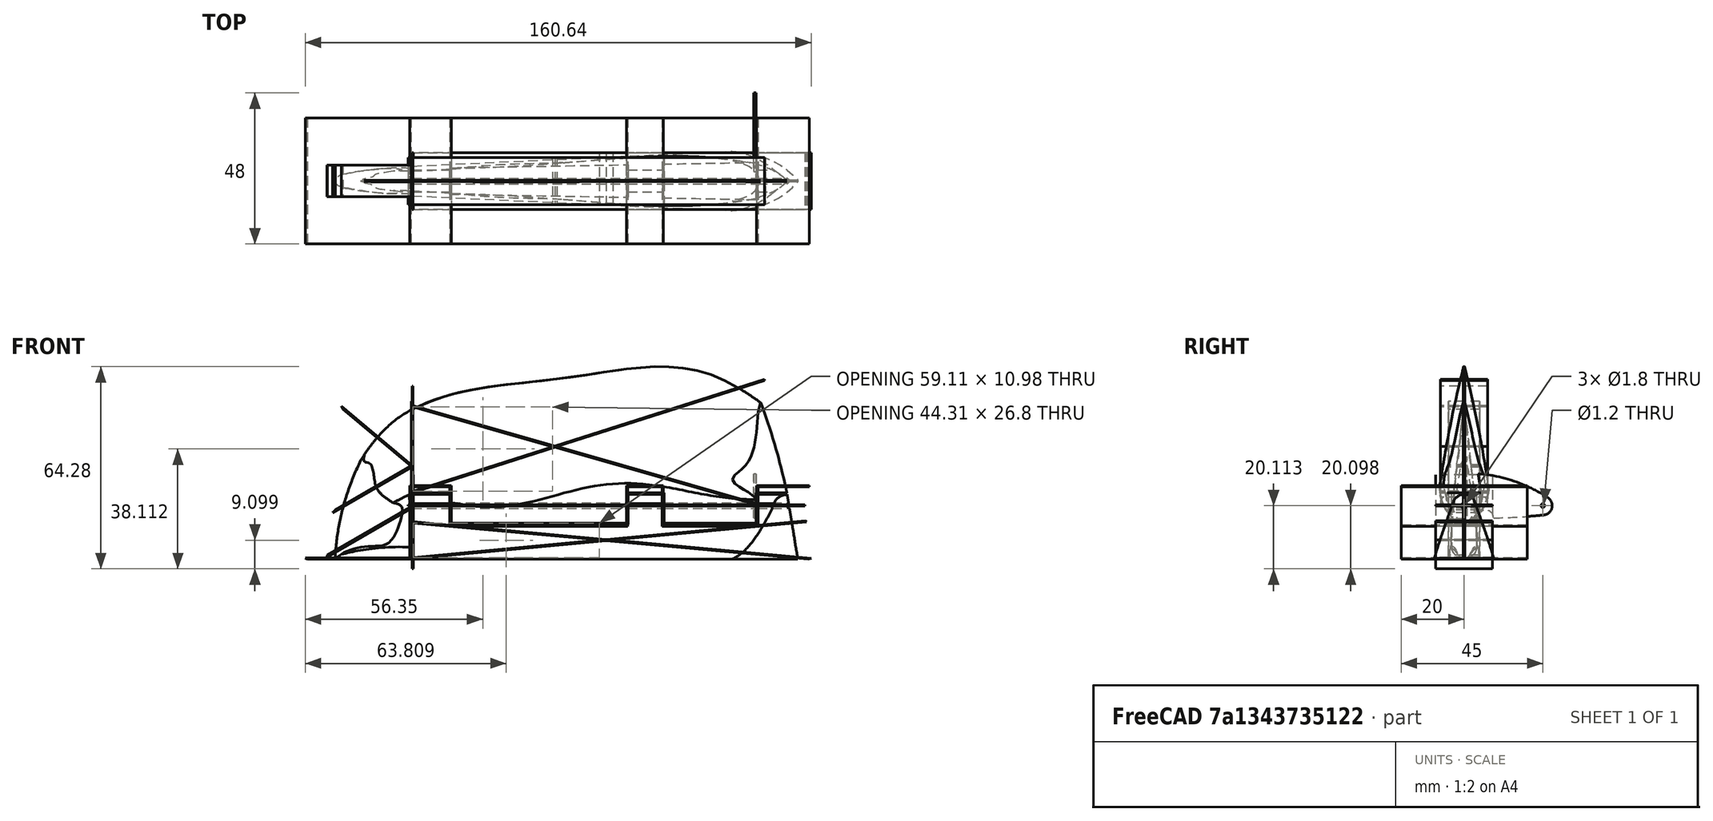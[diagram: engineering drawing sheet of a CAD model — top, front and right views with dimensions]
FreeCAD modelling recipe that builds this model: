
FCSTD DOCUMENT  (FreeCAD 0.20R29410 (Git))
Label: ruddersplit
License: All rights reserved
LicenseURL: http://en.wikipedia.org/wiki/All_rights_reserved
objects: Sketcher::SketchObject×34, PartDesign::Plane×8, PartDesign::Body×8, Mesh::Feature×7, PartDesign::Pad×5, PartDesign::Pocket×5, PartDesign::ShapeBinder×4, PartDesign::AdditiveLoft×3, PartDesign::SubtractiveLoft×3, PartDesign::FeatureBase×1, App::Part×1
note: 87 computed .brp shape members not serialized (recipe doc carries the construction recipe); baked Part::Feature solids carry a one-line shape summary decoded from their .brp

FEATURE [Mesh::Feature] Ta152_rudder  label="Ta152 rudder"
FEATURE [Sketcher::SketchObject] Sketch
  FullyConstrained = false
  MapMode = 5
  Placement = pos=(0,0,0) rot=(1,0,0;1.5708rad)
  Support = -> [XZ_Plane]
  sketch-geometry (24):
    g0: LineSegment StartX=624.263 StartY=141.903 StartZ=0 EndX=657.263 EndY=141.903 EndZ=0
    g1: LineSegment StartX=657.263 StartY=141.903 StartZ=0 EndX=657.263 EndY=164.903 EndZ=0
    g2: LineSegment StartX=657.263 StartY=164.903 StartZ=0 EndX=669.563 EndY=164.903 EndZ=0
    g3: LineSegment StartX=669.563 StartY=164.903 StartZ=0 EndX=669.563 EndY=152.313 EndZ=0
    g4: LineSegment StartX=669.563 StartY=152.313 StartZ=0 EndX=726.093 EndY=152.313 EndZ=0
    g5: LineSegment StartX=726.093 StartY=152.313 StartZ=0 EndX=726.093 EndY=164.903 EndZ=0
    g6: LineSegment StartX=726.093 StartY=164.903 StartZ=0 EndX=736.993 EndY=164.903 EndZ=0
    g7: LineSegment StartX=736.993 StartY=164.903 StartZ=0 EndX=736.993 EndY=152.313 EndZ=0
    g8: LineSegment StartX=736.993 StartY=152.313 StartZ=0 EndX=767.393 EndY=152.313 EndZ=0
    g9: LineSegment StartX=767.393 StartY=152.313 StartZ=0 EndX=767.393 EndY=164.903 EndZ=0
    g10: LineSegment StartX=767.393 StartY=164.903 StartZ=0 EndX=783.71 EndY=164.903 EndZ=0
    g11: LineSegment StartX=624.263 StartY=141.903 StartZ=0 EndX=623.694 EndY=142.303 EndZ=0
    g12: LineSegment StartX=623.694 StartY=142.303 StartZ=0 EndX=656.863 EndY=142.303 EndZ=0
    g13: LineSegment StartX=656.863 StartY=142.303 StartZ=0 EndX=656.863 EndY=165.303 EndZ=0
    g14: LineSegment StartX=656.863 StartY=165.303 StartZ=0 EndX=670.063 EndY=165.303 EndZ=0
    g15: LineSegment StartX=670.063 StartY=165.303 StartZ=0 EndX=670.063 EndY=152.713 EndZ=0
    g16: LineSegment StartX=670.063 StartY=152.713 StartZ=0 EndX=725.693 EndY=152.713 EndZ=0
    g17: LineSegment StartX=725.693 StartY=152.713 StartZ=0 EndX=725.693 EndY=165.303 EndZ=0
    g18: LineSegment StartX=725.693 StartY=165.303 StartZ=0 EndX=737.393 EndY=165.303 EndZ=0
    g19: LineSegment StartX=737.393 StartY=165.303 StartZ=0 EndX=737.393 EndY=152.713 EndZ=0
    g20: LineSegment StartX=737.393 StartY=152.713 StartZ=0 EndX=766.993 EndY=152.713 EndZ=0
    g21: LineSegment StartX=766.993 StartY=152.713 StartZ=0 EndX=766.993 EndY=165.303 EndZ=0
    g22: LineSegment StartX=766.993 StartY=165.303 StartZ=0 EndX=783.71 EndY=165.303 EndZ=0
    g23: LineSegment StartX=783.71 StartY=165.303 StartZ=0 EndX=783.71 EndY=164.903 EndZ=0
  constraints (70):
    c: Coincident(g0,g1)
    c: Coincident(g1,g2)
    c: Horizontal(g2)
    c: Coincident(g2,g3)
    c: Coincident(g3,g4)
    c: Horizontal(g4)
    c: Coincident(g4,g5)
    c: Coincident(g5,g6)
    c: Horizontal(g6)
    c: Coincident(g6,g7)
    c: Vertical(g7)
    c: Coincident(g7,g8)
    c: Horizontal(g8)
    c: Coincident(g8,g9)
    c: Vertical(g9)
    c: Coincident(g9,g10)
    c: Horizontal(g10)
    c: Vertical(g1)
    c: Vertical(g3)
    c: Vertical(g5)
    c: Horizontal(g0)
    c: Horizontal(g4,g7)
    c: Horizontal(g9,g6)
    c: Horizontal(g5,g2)
    c: Coincident(g0,g11)
    c: Coincident(g11,g12)
    c: Horizontal(g12)
    c: Coincident(g12,g13)
    c: Vertical(g13)
    c: Coincident(g13,g14)
    c: Horizontal(g14)
    c: Coincident(g14,g15)
    c: Vertical(g15)
    c: Coincident(g15,g16)
    c: Horizontal(g16)
    c: Coincident(g16,g17)
    c: Vertical(g17)
    c: Coincident(g17,g18)
    c: Horizontal(g18)
    c: Coincident(g18,g19)
    c: Vertical(g19)
    c: Coincident(g19,g20)
    c: Horizontal(g20)
    c: Coincident(g20,g21)
    c: Vertical(g21)
    c: Coincident(g21,g22)
    c: Horizontal(g22)
    c: Coincident(g22,g23)
    c: Coincident(g23,g10)
    c: Vertical(g23)
    c: DistanceY(g0,g12) = 0.4
    c: DistanceX(g13,g1) = 0.4
    c: DistanceX(g2,g14) = 0.5
    c: DistanceY(g1,g13) = 0.4
    c: DistanceY(g3,g15) = 0.4
    c: DistanceX(g17,g5) = 0.4
    c: DistanceX(g6,g18) = 0.4
    c: Horizontal(g16,g19)
    c: Horizontal(g17,g14)
    c: Horizontal(g21,g18)
    c: DistanceX(g20,g8) = 0.4
    c: DistanceX(g0) = 624.263
    c: DistanceY(g0) = 141.903
    c: DistanceX(g0,g0) = 33  'Length1'
    c: DistanceY(g1,g1) = 23  'Height1'
    c: DistanceX(g2,g2) = 12.3  'Length2'
    c: DistanceY(g0,g3) = 10.41  'Hinge height'
    c: DistanceX(g4,g4) = 56.53  'Length3'
    c: DistanceX(g6,g6) = 10.9  'length4'
    c: DistanceX(g8,g8) = 30.4  'length5'
FEATURE [PartDesign::Pad] Pad
  Direction = (0,-1,-2e-16)
  Length = 40
  Length2 = 10
  Midplane = true
  Placement = pos=(0,0,0) rot=(1,0,0;1.5708rad)
  Profile = -> Sketch
  ReferenceAxis = -> Sketch [N_Axis]
  Type = 0
FEATURE [Sketcher::SketchObject] Sketch001
  FullyConstrained = true
  MapMode = 5
  Placement = pos=(624.263,-9e-16,141.903) rot=(0,1,0;3.14159rad)
FEATURE [PartDesign::Plane] DatumPlane001
  Length = 719.203
  MapMode = 7
  Placement = pos=(657.263,-20,141.903) rot=(0,1,0;3.14159rad)
  ResizeMode = 0
  Support = -> [Pad]
  Width = 86.9395
FEATURE [PartDesign::Plane] DatumPlane
  AttachmentOffset = pos=(-34,0,0) rot=(0,1,0;1.5708rad)
  Length = 68.2922
  MapMode = 45
  Placement = pos=(657.694,8.98e-14,142.303) rot=(-0.57735,0.57735,0.57735;4.18879rad)
  ResizeMode = 0
  Support = -> [Pad]
  Width = 185.595
FEATURE [Sketcher::SketchObject] Sketch002  label="Hingetop"
  FullyConstrained = false
  MapMode = 5
  Placement = pos=(657.694,8.98e-14,142.303) rot=(0.57735,-0.57735,-0.57735;2.0944rad)
  Support = -> [DatumPlane]
  sketch-geometry (5):
    g0: ArcOfCircle CenterX=0 CenterY=16.5851 CenterZ=0 NormalX=0 NormalY=0 NormalZ=1 AngleXU=0 Radius=3.59111 StartAngle=0.199351 EndAngle=2.94224
    g1: LineSegment StartX=-4.713 StartY=-0.4 StartZ=0 EndX=6.72755 EndY=-0.4 EndZ=0
    g2: LineSegment StartX=-3.51999 StartY=17.2962 StartZ=0 EndX=-4.713 EndY=-0.4 EndZ=0
    g3: LineSegment StartX=3.51999 StartY=17.2962 StartZ=0 EndX=4.713 EndY=-0.4 EndZ=0
    g4: LineSegment StartX=-4.713 StartY=-0.4 StartZ=0 EndX=4.713 EndY=-0.4 EndZ=0
  constraints (9):
    c: Horizontal(g0,g0)
    c: PointOnObject(g0,g-2)
    c: Horizontal(g1)
    c: DistanceY(g1,g-1) = 0.4
    c: Coincident(g2,g0)
    c: Coincident(g2,g1)
    c: Coincident(g4,g2)
    c: Coincident(g4,g3)
    c: Horizontal(g4)
FEATURE [Sketcher::SketchObject] Sketch003  label="Hingebottom"
  AttachmentOffset = pos=(0,0,-124) rot=(0,0,1;0rad)
  FullyConstrained = false
  MapMode = 5
  Placement = pos=(781.694,3.926e-13,142.303) rot=(0.57735,-0.57735,-0.57735;2.0944rad)
  Support = -> [DatumPlane]
  sketch-geometry (5):
    g0: ArcOfCircle CenterX=0 CenterY=16.5851 CenterZ=0 NormalX=0 NormalY=0 NormalZ=1 AngleXU=0 Radius=3.59111 StartAngle=0.199351 EndAngle=2.94224
    g1: LineSegment StartX=-9.5 StartY=-0.4 StartZ=0 EndX=6.72755 EndY=-0.4 EndZ=0
    g2: LineSegment StartX=-3.51999 StartY=17.2962 StartZ=0 EndX=-9.5 EndY=-0.4 EndZ=0
    g3: LineSegment StartX=3.51999 StartY=17.2962 StartZ=0 EndX=9.5 EndY=-0.4 EndZ=0
    g4: LineSegment StartX=-9.5 StartY=-0.4 StartZ=0 EndX=9.5 EndY=-0.4 EndZ=0
  constraints (10):
    c: Horizontal(g0,g0)
    c: PointOnObject(g0,g-2)
    c: Horizontal(g1)
    c: DistanceY(g1,g-1) = 0.4
    c: Coincident(g2,g0)
    c: Coincident(g2,g1)
    c: Coincident(g4,g2)
    c: Coincident(g4,g3)
    c: Symmetric(g2,g3,g-2)
    c: DistanceX(g4,g4) = 19
FEATURE [PartDesign::Body] Body
  Group = -> [Sketch,Pad,Sketch001,DatumPlane001,DatumPlane,Sketch002,Sketch003]
  Origin = -> Origin
  Tip = -> Pad
FEATURE [Sketcher::SketchObject] Sketch004  label="Hingetop001"
  FullyConstrained = false
  MapMode = 5
  Placement = pos=(657.694,8.98e-14,142.303) rot=(0.57735,-0.57735,-0.57735;2.0944rad)
  Support = -> [DatumPlane]
  sketch-geometry (6):
    g0: ArcOfCircle CenterX=0 CenterY=16.5851 CenterZ=0 NormalX=0 NormalY=0 NormalZ=1 AngleXU=0 Radius=3.59111 StartAngle=0.199351 EndAngle=2.94224
    g1: LineSegment StartX=-4.713 StartY=-0.4 StartZ=0 EndX=6.72755 EndY=-0.4 EndZ=0
    g2: LineSegment StartX=-3.51999 StartY=17.2962 StartZ=0 EndX=-4.713 EndY=-0.4 EndZ=0
    g3: LineSegment StartX=3.51999 StartY=17.2962 StartZ=0 EndX=4.713 EndY=-0.4 EndZ=0
    g4: LineSegment StartX=-4.713 StartY=-0.4 StartZ=0 EndX=4.713 EndY=-0.4 EndZ=0
    g5: Circle CenterX=0 CenterY=16.5851 CenterZ=0 NormalX=0 NormalY=0 NormalZ=1 AngleXU=0 Radius=0.9
  constraints (12):
    c: Horizontal(g0,g0)
    c: PointOnObject(g0,g-2)
    c: Horizontal(g1)
    c: DistanceY(g1,g-1) = 0.4
    c: Coincident(g2,g0)
    c: Coincident(g2,g1)
    c: Coincident(g4,g2)
    c: Coincident(g4,g3)
    c: Horizontal(g4)
    c: DistanceY(g0) = 16.5851
    c: Coincident(g5,g0)
    c: Diameter(g5) = 1.8
FEATURE [Sketcher::SketchObject] Sketch005  label="Hingebottom001"
  AttachmentOffset = pos=(0,0,-124) rot=(0,0,1;0rad)
  FullyConstrained = false
  MapMode = 5
  Placement = pos=(781.694,3.926e-13,142.303) rot=(0.57735,-0.57735,-0.57735;2.0944rad)
  Support = -> [DatumPlane]
  sketch-geometry (6):
    g0: ArcOfCircle CenterX=0 CenterY=16.5851 CenterZ=0 NormalX=0 NormalY=0 NormalZ=1 AngleXU=0 Radius=3.59111 StartAngle=0.199351 EndAngle=2.94224
    g1: LineSegment StartX=-10.5 StartY=-0.4 StartZ=0 EndX=6.72755 EndY=-0.4 EndZ=0
    g2: LineSegment StartX=-3.51999 StartY=17.2962 StartZ=0 EndX=-10.5 EndY=-0.4 EndZ=0
    g3: LineSegment StartX=3.51999 StartY=17.2962 StartZ=0 EndX=10.5 EndY=-0.4 EndZ=0
    g4: LineSegment StartX=-10.5 StartY=-0.4 StartZ=0 EndX=10.5 EndY=-0.4 EndZ=0
    g5: Circle CenterX=0 CenterY=16.5851 CenterZ=0 NormalX=0 NormalY=0 NormalZ=1 AngleXU=0 Radius=0.9
  constraints (13):
    c: Horizontal(g0,g0)
    c: PointOnObject(g0,g-2)
    c: Horizontal(g1)
    c: DistanceY(g1,g-1) = 0.4
    c: Coincident(g2,g0)
    c: Coincident(g2,g1)
    c: Coincident(g4,g2)
    c: Coincident(g4,g3)
    c: Symmetric(g2,g3,g-2)
    c: DistanceX(g4,g4) = 21
    c: DistanceY(g0) = 16.5851
    c: Coincident(g5,g0)
    c: Diameter(g5) = 1.8
FEATURE [PartDesign::Plane] CopyDatumPlane001
  Length = 719.203
  Placement = pos=(657.263,-20,141.903) rot=(0,1,0;3.14159rad)
  ResizeMode = 0
  Width = 86.9395
FEATURE [Sketcher::SketchObject] Sketch006
  FullyConstrained = false
  MapMode = 5
  Placement = pos=(657.263,-20,141.903) rot=(0,1,0;3.14159rad)
  Support = -> [CopyDatumPlane001]
  sketch-geometry (21):
    g0-g6: Circle x7 (B-spline internal-alignment scaffolding for g7; pole/knot coordinates omitted)
    g7: BSplineCurve PolesCount=7 KnotsCount=5 Degree=3 IsPeriodic=0
    g8-g11: GeomPoint x4 (B-spline internal-alignment scaffolding for g7; pole/knot coordinates omitted)
    g12: GeomPoint X=-122.781 Y=20.25 Z=0
    g13: LineSegment StartX=-122.783 StartY=20.25 StartZ=0 EndX=-122.783 EndY=19.7442 EndZ=0
    g14: LineSegment StartX=-83.4528 StartY=29.2883 StartZ=0 EndX=-83.4528 EndY=61.9285 EndZ=0
    g15: LineSegment StartX=-83.4528 StartY=61.9285 StartZ=0 EndX=-142.52 EndY=61.9285 EndZ=0
    g16: LineSegment StartX=-142.52 StartY=61.9285 StartZ=0 EndX=-142.52 EndY=-14.2649 EndZ=0
    g17: LineSegment StartX=-142.52 StartY=-14.2649 StartZ=0 EndX=-83.4528 EndY=-14.2649 EndZ=0
    g18: LineSegment StartX=-83.4528 StartY=-14.2649 StartZ=0 EndX=-83.4528 EndY=10.7059 EndZ=0
    g19: LineSegment StartX=-120.634 StartY=19.9971 StartZ=0 EndX=-124.073 EndY=19.9971 EndZ=0
    g20: BSplineCurve PolesCount=7 KnotsCount=5 Degree=3 IsPeriodic=0
  constraints (11):
    c: Weight(g0) = 1
    c: Equal(g0, g1-g6) x6
    c: InternalAlignment(g0-g6 -> g7) x7
    c: InternalAlignment(g8-g11 -> g7) x4
    c: Horizontal(g17)
    c: Coincident(g17,g18)
    c: Vertical(g18)
    c: Horizontal(g19)
    c: Symmetric(g13,g7,g19)
    c: Coincident(g20,g18)
    c: Coincident(g13,g20)
FEATURE [PartDesign::Plane] CopyDatumPlane002
  Length = 719.199
  Placement = pos=(657.26,-20,162.9) rot=(0,1,0;3.14159rad)
  ResizeMode = 0
  Width = 86.9394
FEATURE [Sketcher::SketchObject] Sketch007
  FullyConstrained = false
  MapMode = 5
  Placement = pos=(657.26,-20,162.9) rot=(0,1,0;3.14159rad)
  Support = -> [CopyDatumPlane002]
  sketch-geometry (21):
    g0-g3: Circle x4 (B-spline internal-alignment scaffolding for g4; pole/knot coordinates omitted)
    g4: BSplineCurve PolesCount=7 KnotsCount=5 Degree=3 IsPeriodic=0
    g5-g8: GeomPoint x4 (B-spline internal-alignment scaffolding for g4; pole/knot coordinates omitted)
    g9: Circle CenterX=-74.5909 CenterY=27.8004 CenterZ=0 NormalX=0 NormalY=0 NormalZ=1 AngleXU=0 Radius=1
    g10: Circle CenterX=-87.7384 CenterY=27.8332 CenterZ=0 NormalX=0 NormalY=0 NormalZ=1 AngleXU=0 Radius=1
    g11: Circle CenterX=-99.3594 CenterY=27.6151 CenterZ=0 NormalX=0 NormalY=0 NormalZ=1 AngleXU=0 Radius=1
    g12: GeomPoint X=-79.145 Y=27.8076 Z=0
    g13: LineSegment StartX=-119.344 StartY=20.2366 StartZ=0 EndX=-119.344 EndY=19.7468 EndZ=0
    g14: LineSegment StartX=-122.669 StartY=19.9917 StartZ=0 EndX=-115.003 EndY=19.9917 EndZ=0
    g15: BSplineCurve PolesCount=7 KnotsCount=5 Degree=3 IsPeriodic=0
    g16: LineSegment StartX=-68.8738 StartY=27.5511 StartZ=0 EndX=-68.8738 EndY=47.5798 EndZ=0
    g17: LineSegment StartX=-68.8738 StartY=47.5798 StartZ=0 EndX=-137.844 EndY=47.5798 EndZ=0
    g18: LineSegment StartX=-137.844 StartY=47.5798 StartZ=0 EndX=-137.844 EndY=-8.4859 EndZ=0
    g19: LineSegment StartX=-137.844 StartY=-8.4859 StartZ=0 EndX=-68.8738 EndY=-8.4859 EndZ=0
    g20: LineSegment StartX=-68.8738 StartY=-8.4859 StartZ=0 EndX=-68.8738 EndY=12.4323 EndZ=0
  constraints (25):
    c: Weight(g0) = 1
    c: Equal(g0,g1)
    c: Equal(g0,g2)
    c: Equal(g0,g3)
    c: InternalAlignment(g0-g3 -> g4) x4
    c: InternalAlignment(g5-g9 -> g4) x5
    c: Equal(g9,g0)
    c: InternalAlignment(g10,g4)
    c: Equal(g10,g0)
    c: Equal(g11,g0)
    c: InternalAlignment(g12,g4)
    c: Coincident(g13,g4)
    c: Horizontal(g14)
    c: Symmetric(g13,g4,g14)
    c: Coincident(g16,g4)
    c: Vertical(g16)
    c: Coincident(g16,g17)
    c: Horizontal(g17)
    c: Coincident(g17,g18)
    c: Vertical(g18)
    c: Coincident(g18,g19)
    c: Horizontal(g19)
    c: Coincident(g19,g20)
    c: Vertical(g20)
    c: Coincident(g15,g20)
FEATURE [Sketcher::SketchObject] Sketch008
  FullyConstrained = false
  MapMode = 5
  Placement = pos=(0,0,0) rot=(1,0,0;1.5708rad)
  Support = -> [XZ_Plane005]
  sketch-geometry (17):
    g0: LineSegment StartX=726.116 StartY=153.482 StartZ=0 EndX=726.116 EndY=229.788 EndZ=0
    g1: LineSegment StartX=669.49 StartY=153.672 StartZ=0 EndX=669.49 EndY=227.56 EndZ=0
    g2: LineSegment StartX=767.362 StartY=153.926 StartZ=0 EndX=767.362 EndY=224.102 EndZ=0
    g3: LineSegment StartX=725.987 StartY=152.316 StartZ=0 EndX=584.529 EndY=152.316 EndZ=0
    g4: LineSegment StartX=789.185 StartY=149.038 StartZ=0 EndX=782.856 EndY=164.717 EndZ=0
    g5: LineSegment StartX=782.856 StartY=164.717 StartZ=0 EndX=767.362 EndY=164.717 EndZ=0
    g6: LineSegment StartX=767.362 StartY=164.717 StartZ=0 EndX=767.362 EndY=152.912 EndZ=0
    g7: LineSegment StartX=767.362 StartY=152.912 StartZ=0 EndX=737.052 EndY=152.912 EndZ=0
    g8: LineSegment StartX=737.052 StartY=152.912 StartZ=0 EndX=737.052 EndY=166.962 EndZ=0
    g9: LineSegment StartX=737.052 StartY=166.962 StartZ=0 EndX=726.116 EndY=166.962 EndZ=0
    g10: LineSegment StartX=726.116 StartY=166.962 StartZ=0 EndX=726.116 EndY=152.912 EndZ=0
    g11: LineSegment StartX=726.116 StartY=152.912 StartZ=0 EndX=669.49 EndY=152.912 EndZ=0
    g12: LineSegment StartX=669.49 StartY=152.912 StartZ=0 EndX=669.49 EndY=166.268 EndZ=0
    g13: LineSegment StartX=669.49 StartY=166.268 StartZ=0 EndX=654.865 EndY=166.268 EndZ=0
    g14: LineSegment StartX=654.865 StartY=166.268 StartZ=0 EndX=654.865 EndY=181.772 EndZ=0
    g15: LineSegment StartX=654.865 StartY=181.772 StartZ=0 EndX=794.924 EndY=181.772 EndZ=0
    g16: LineSegment StartX=794.924 StartY=181.772 StartZ=0 EndX=789.185 EndY=149.038 EndZ=0
  constraints (32):
    c: Vertical(g0)
    c: Vertical(g1)
    c: Vertical(g2)
    c: Horizontal(g3)
    c: Coincident(g4,g5)
    c: PointOnObject(g5,g2)
    c: Horizontal(g5)
    c: Coincident(g5,g6)
    c: Vertical(g6)
    c: Coincident(g6,g7)
    c: Horizontal(g7)
    c: Coincident(g7,g8)
    c: Vertical(g8)
    c: Coincident(g8,g9)
    c: PointOnObject(g9,g0)
    c: Horizontal(g9)
    c: Coincident(g9,g10)
    c: Vertical(g10)
    c: Coincident(g10,g11)
    c: Horizontal(g11)
    c: Coincident(g11,g12)
    c: PointOnObject(g12,g1)
    c: Vertical(g12)
    c: Coincident(g12,g13)
    c: Horizontal(g13)
    c: Coincident(g13,g14)
    c: Vertical(g14)
    c: Coincident(g14,g15)
    c: Horizontal(g15)
    c: Coincident(g15,g16)
    c: Coincident(g16,g4)
    c: Horizontal(g10,g7)
FEATURE [Sketcher::SketchObject] Sketch017  label="SubLft2"
  AttachmentOffset = pos=(0,0,168) rot=(0,0,1;0rad)
  FullyConstrained = false
  MapMode = 5
  Placement = pos=(0,0,168) rot=(0,0,1;0rad)
  Support = -> [XY_Plane002]
  sketch-geometry (28):
    g0-g5: Circle x6 (B-spline internal-alignment scaffolding for g6; pole/knot coordinates omitted)
    g6: BSplineCurve PolesCount=6 KnotsCount=4 Degree=3 IsPeriodic=0
    g7-g10: GeomPoint x4 (B-spline internal-alignment scaffolding for g6; pole/knot coordinates omitted)
    g11-g16: Circle x6 (B-spline internal-alignment scaffolding for g17; pole/knot coordinates omitted)
    g17: BSplineCurve PolesCount=6 KnotsCount=4 Degree=3 IsPeriodic=0
    g18-g21: GeomPoint x4 (B-spline internal-alignment scaffolding for g17; pole/knot coordinates omitted)
    g22: LineSegment StartX=757.877 StartY=6.51924 StartZ=0 EndX=757.877 EndY=27.4666 EndZ=0
    g23: LineSegment StartX=757.877 StartY=27.4666 StartZ=0 EndX=799.809 EndY=27.4666 EndZ=0
    g24: LineSegment StartX=799.809 StartY=27.4666 StartZ=0 EndX=799.809 EndY=-22.2115 EndZ=0
    g25: LineSegment StartX=799.809 StartY=-22.2115 StartZ=0 EndX=757.877 EndY=-22.2115 EndZ=0
    g26: LineSegment StartX=757.877 StartY=-22.2115 StartZ=0 EndX=757.877 EndY=-6.51924 EndZ=0
    g27: LineSegment StartX=775.463 StartY=0.225 StartZ=0 EndX=775.463 EndY=-0.225 EndZ=0
  constraints (28):
    c: Weight(g0) = 1
    c: Equal(g0, g1-g5) x5
    c: InternalAlignment(g0-g5 -> g6) x6
    c: InternalAlignment(g7-g10 -> g6) x4
    c: Weight(g11) = 1
    c: Equal(g11, g12-g16) x5
    c: InternalAlignment(g11-g16 -> g17) x6
    c: InternalAlignment(g18-g21 -> g17) x4
    c: Symmetric(g15,g4,g-1)
    c: Symmetric(g3,g14,g-1)
    c: Symmetric(g2,g13,g-1)
    c: Symmetric(g12,g1,g-1)
    c: Coincident(g22,g6)
    c: Vertical(g22)
    c: Coincident(g22,g23)
    c: Horizontal(g23)
    c: Coincident(g23,g24)
    c: Vertical(g24)
    c: Coincident(g24,g25)
    c: Horizontal(g25)
    c: Coincident(g25,g26)
    c: Coincident(g26,g17)
    c: Vertical(g26)
    c: DistanceY(g27,g27) = 0.45
    c: Symmetric(g27,g27,g-1)
    c: Symmetric(g17,g6,g-1)
    c: Coincident(g6,g27)
    c: Symmetric(g6,g17,g-1)
FEATURE [Sketcher::SketchObject] Sketch018  label="SubLft3"
  AttachmentOffset = pos=(0,0,202) rot=(0,0,1;0rad)
  FullyConstrained = false
  MapMode = 5
  Placement = pos=(0,0,202) rot=(0,0,1;0rad)
  Support = -> [XY_Plane002]
  sketch-geometry (28):
    g0-g5: Circle x6 (B-spline internal-alignment scaffolding for g6; pole/knot coordinates omitted)
    g6: BSplineCurve PolesCount=6 KnotsCount=4 Degree=3 IsPeriodic=0
    g7-g10: GeomPoint x4 (B-spline internal-alignment scaffolding for g6; pole/knot coordinates omitted)
    g11-g16: Circle x6 (B-spline internal-alignment scaffolding for g17; pole/knot coordinates omitted)
    g17: BSplineCurve PolesCount=6 KnotsCount=4 Degree=3 IsPeriodic=0
    g18-g21: GeomPoint x4 (B-spline internal-alignment scaffolding for g17; pole/knot coordinates omitted)
    g22: LineSegment StartX=743.122 StartY=5 StartZ=0 EndX=743.122 EndY=22.4962 EndZ=0
    g23: LineSegment StartX=743.122 StartY=22.4962 StartZ=0 EndX=772.321 EndY=22.4962 EndZ=0
    g24: LineSegment StartX=772.321 StartY=22.4962 StartZ=0 EndX=772.321 EndY=-24.1809 EndZ=0
    g25: LineSegment StartX=772.321 StartY=-24.1809 StartZ=0 EndX=743.122 EndY=-24.1809 EndZ=0
    g26: LineSegment StartX=743.122 StartY=-24.1809 StartZ=0 EndX=743.122 EndY=-5 EndZ=0
    g27: LineSegment StartX=763.974 StartY=0.225 StartZ=0 EndX=763.974 EndY=-0.225 EndZ=0
  constraints (33):
    c: Weight(g0) = 1
    c: Equal(g0, g1-g5) x5
    c: InternalAlignment(g0-g5 -> g6) x6
    c: InternalAlignment(g7-g10 -> g6) x4
    c: Weight(g11) = 1
    c: Equal(g11, g12-g16) x5
    c: InternalAlignment(g11-g16 -> g17) x6
    c: InternalAlignment(g18-g21 -> g17) x4
    c: Symmetric(g15,g4,g-1)
    c: Symmetric(g3,g14,g-1)
    c: Symmetric(g2,g13,g-1)
    c: Symmetric(g12,g1,g-1)
    c: Coincident(g22,g6)
    c: Vertical(g22)
    c: Coincident(g22,g23)
    c: Horizontal(g23)
    c: Coincident(g23,g24)
    c: Vertical(g24)
    c: Coincident(g25,g26)
    c: Coincident(g26,g17)
    c: Vertical(g26)
    c: Symmetric(g6,g17,g-1)
    c: Symmetric(g6,g17,g-1)
    c: Coincident(g27,g6)
    c: Coincident(g27,g17)
    c: DistanceY(g27,g27) = 0.45
    c: DistanceY(g17,g6) = 10
    c: DistanceY(g15,g4) = 9
    c: DistanceY(g14,g3) = 7
    c: DistanceY(g13,g2) = 5
    c: DistanceY(g12,g1) = 3
    c: Coincident(g24,g25)
    c: Horizontal(g25)
FEATURE [PartDesign::FeatureBase] BaseFeature
  BaseFeature = -> DatumPlane
FEATURE [PartDesign::AdditiveLoft] AdditiveLoft
  BaseFeature = -> BaseFeature
  Closed = false
  Profile = -> Sketch004
  Ruled = false
  Sections = -> [Sketch005]
FEATURE [PartDesign::SubtractiveLoft] SubtractiveLoft
  BaseFeature = -> AdditiveLoft
  Closed = false
  Profile = -> Sketch006
  Ruled = false
  Sections = -> [Sketch007]
FEATURE [PartDesign::Pocket] Pocket
  BaseFeature = -> SubtractiveLoft
  Direction = (0,1,2e-16)
  Length = 15
  Length2 = 5
  Midplane = true
  Profile = -> Sketch008
  ReferenceAxis = -> Sketch008 [N_Axis]
  Type = 0
FEATURE [PartDesign::Body] Body001
  Origin = -> Origin001
  Tip = -> Pocket
FEATURE [Sketcher::SketchObject] Sketch009  label="Top Sk"
  ExternalGeometry = -> [Pocket]
  FullyConstrained = false
  Placement = pos=(657.694,9e-14,142.303) rot=(-0.57735,0.57735,0.57735;4.18879rad)
  sketch-geometry (26):
    g0: LineSegment StartX=-0.225 StartY=47.2182 StartZ=0 EndX=0.225 EndY=47.2182 EndZ=0
    g1: LineSegment StartX=-6.39707 StartY=10.7302 StartZ=0 EndX=5.82884 EndY=10.7302 EndZ=0
    g2: LineSegment StartX=-0.2 StartY=10.961 StartZ=0 EndX=0.2 EndY=10.961 EndZ=0
    g3: Circle CenterX=0 CenterY=16.5851 CenterZ=0 NormalX=0 NormalY=0 NormalZ=1 AngleXU=0 Radius=0.9
    g4: Circle CenterX=-3.51999 CenterY=17.2962 CenterZ=0 NormalX=0 NormalY=0 NormalZ=1 AngleXU=0 Radius=1
    g5: Circle CenterX=-3.03433 CenterY=15.3419 CenterZ=0 NormalX=0 NormalY=0 NormalZ=1 AngleXU=0 Radius=1
    g6: Circle CenterX=-2.07711 CenterY=12.9545 CenterZ=0 NormalX=0 NormalY=0 NormalZ=1 AngleXU=0 Radius=1
    g7: Circle CenterX=-0.984759 CenterY=11.4792 CenterZ=0 NormalX=0 NormalY=0 NormalZ=1 AngleXU=0 Radius=1
    g8: Circle CenterX=-0.2 CenterY=10.7498 CenterZ=0 NormalX=0 NormalY=0 NormalZ=1 AngleXU=0 Radius=1
    g9: BSplineCurve PolesCount=5 KnotsCount=3 Degree=3 IsPeriodic=0
    g10: GeomPoint X=-3.51999 Y=17.2962 Z=0
    g11: GeomPoint X=-2.04333 Y=13.1825 Z=0
    g12: GeomPoint X=-0.2 Y=10.7498 Z=0
    g13: Circle CenterX=-3.51999 CenterY=17.2962 CenterZ=0 NormalX=0 NormalY=0 NormalZ=1 AngleXU=0 Radius=1
    g14: Circle CenterX=-3.08825 CenterY=22.649 CenterZ=0 NormalX=0 NormalY=0 NormalZ=1 AngleXU=0 Radius=1
    g15: Circle CenterX=-2.54219 CenterY=27.5596 CenterZ=0 NormalX=0 NormalY=0 NormalZ=1 AngleXU=0 Radius=1
    g16: Circle CenterX=-1.90148 CenterY=32.5914 CenterZ=0 NormalX=0 NormalY=0 NormalZ=1 AngleXU=0 Radius=1
    g17: Circle CenterX=-1.15109 CenterY=38.9635 CenterZ=0 NormalX=0 NormalY=0 NormalZ=1 AngleXU=0 Radius=1
    g18: Circle CenterX=-0.225 CenterY=47.2182 CenterZ=0 NormalX=0 NormalY=0 NormalZ=1 AngleXU=0 Radius=1
    g19: BSplineCurve PolesCount=6 KnotsCount=4 Degree=3 IsPeriodic=0
    g20: GeomPoint X=-3.51999 Y=17.2962 Z=0
    g21: GeomPoint X=-2.57192 Y=27.1706 Z=0
    g22: GeomPoint X=-1.82067 Y=33.3458 Z=0
    g23: GeomPoint X=-0.225 Y=47.2182 Z=0
    g24: BSplineCurve PolesCount=6 KnotsCount=4 Degree=3 IsPeriodic=0
    g25: BSplineCurve PolesCount=5 KnotsCount=3 Degree=3 IsPeriodic=0
  constraints (4):
    c: Coincident(g9,g19)
    c: Coincident(g0,g19)
    c: Coincident(g2,g9)
    c: Coincident(g0,g24)
FEATURE [Sketcher::SketchObject] Sketch010  label="Mid Sk"
  ExternalGeometry = -> [Pocket]
  FullyConstrained = false
  Placement = pos=(716,0,142.3) rot=(0.57735,-0.57735,-0.57735;2.0944rad)
  sketch-geometry (24):
    g0: LineSegment StartX=-0.225 StartY=58.6243 StartZ=0 EndX=0.225 EndY=58.6243 EndZ=0
    g1: LineSegment StartX=-6.39707 StartY=10.7302 StartZ=0 EndX=5.82884 EndY=10.7302 EndZ=0
    g2: LineSegment StartX=-0.2 StartY=10.961 StartZ=0 EndX=0.2 EndY=10.961 EndZ=0
    g3: Circle CenterX=0 CenterY=16.5851 CenterZ=0 NormalX=0 NormalY=0 NormalZ=1 AngleXU=0 Radius=0.9
    g4-g8: Circle x5 (B-spline internal-alignment scaffolding for g9; pole/knot coordinates omitted)
    g9: BSplineCurve PolesCount=5 KnotsCount=3 Degree=3 IsPeriodic=0
    g10: GeomPoint X=-0.2 Y=10.961 Z=0
    g11: GeomPoint X=-5.21976 Y=15.3194 Z=0
    g12: GeomPoint X=-6.64817 Y=22.8932 Z=0
    g13-g17: Circle x5 (B-spline internal-alignment scaffolding for g18; pole/knot coordinates omitted)
    g18: BSplineCurve PolesCount=5 KnotsCount=3 Degree=3 IsPeriodic=0
    g19: GeomPoint X=-6.64817 Y=22.8932 Z=0
    g20: GeomPoint X=-3.37568 Y=40.0934 Z=0
    g21: GeomPoint X=-0.225 Y=58.6243 Z=0
    g22: BSplineCurve PolesCount=5 KnotsCount=3 Degree=3 IsPeriodic=0
    g23: BSplineCurve PolesCount=5 KnotsCount=3 Degree=3 IsPeriodic=0
  constraints (19):
    c: Symmetric(g0,g0,g-2)
    c: Weight(g4) = 1
    c: Coincident(g9,g2)
    c: Equal(g4, g5-g8) x4
    c: InternalAlignment(g4-g8 -> g9) x5
    c: InternalAlignment(g10,g9)
    c: InternalAlignment(g11,g9)
    c: InternalAlignment(g12,g9)
    c: Weight(g13) = 1
    c: Coincident(g18,g9)
    c: Equal(g13, g14-g17) x4
    c: Coincident(g18,g0)
    c: InternalAlignment(g13-g17 -> g18) x5
    c: InternalAlignment(g19,g18)
    c: InternalAlignment(g20,g18)
    c: InternalAlignment(g21,g18)
    c: Coincident(g2,g23)
    c: Coincident(g22,g23)
    c: Coincident(g0,g22)
FEATURE [Sketcher::SketchObject] Sketch011  label="Top Sk2"
  ExternalGeometry = -> [Pocket]
  FullyConstrained = false
  Placement = pos=(671,0,142.3) rot=(0.57735,-0.57735,-0.57735;2.0944rad)
  sketch-geometry (27):
    g0: LineSegment StartX=-0.225 StartY=52.1739 StartZ=0 EndX=0.225 EndY=52.1739 EndZ=0
    g1: LineSegment StartX=-6.39707 StartY=10.7302 StartZ=0 EndX=5.82884 EndY=10.7302 EndZ=0
    g2: LineSegment StartX=-0.2 StartY=10.961 StartZ=0 EndX=0.2 EndY=10.961 EndZ=0
    g3: Circle CenterX=0 CenterY=16.5851 CenterZ=0 NormalX=0 NormalY=0 NormalZ=1 AngleXU=0 Radius=0.9
    g4: GeomPoint X=-0.2 Y=10.7498 Z=0
    g5-g10: Circle x6 (B-spline internal-alignment scaffolding for g11; pole/knot coordinates omitted)
    g11: BSplineCurve PolesCount=6 KnotsCount=4 Degree=3 IsPeriodic=0
    g12-g15: GeomPoint x4 (B-spline internal-alignment scaffolding for g11; pole/knot coordinates omitted)
    g16-g20: Circle x5 (B-spline internal-alignment scaffolding for g21; pole/knot coordinates omitted)
    g21: BSplineCurve PolesCount=5 KnotsCount=3 Degree=3 IsPeriodic=0
    g22: GeomPoint X=-3.91424 Y=17.3593 Z=0
    g23: GeomPoint X=-2.43471 Y=13.0632 Z=0
    g24: GeomPoint X=-0.2 Y=10.961 Z=0
    g25: BSplineCurve PolesCount=6 KnotsCount=4 Degree=3 IsPeriodic=0
    g26: BSplineCurve PolesCount=5 KnotsCount=3 Degree=3 IsPeriodic=0
  constraints (16):
    c: Symmetric(g0,g0,g-2)
    c: Weight(g5) = 1
    c: Equal(g5, g6-g10) x5
    c: Coincident(g11,g0)
    c: InternalAlignment(g5-g10 -> g11) x6
    c: InternalAlignment(g12-g15 -> g11) x4
    c: Weight(g16) = 1
    c: Coincident(g21,g11)
    c: Equal(g16, g17-g20) x4
    c: Coincident(g21,g2)
    c: InternalAlignment(g16-g20 -> g21) x5
    c: InternalAlignment(g22,g21)
    c: InternalAlignment(g23,g21)
    c: InternalAlignment(g24,g21)
    c: Coincident(g2,g26)
    c: Coincident(g0,g25)
FEATURE [Sketcher::SketchObject] Sketch012  label="Mid Sk2"
  ExternalGeometry = -> [Pocket]
  FullyConstrained = false
  Placement = pos=(740,0,142.3) rot=(0.57735,-0.57735,-0.57735;2.0944rad)
  sketch-geometry (22):
    g0: LineSegment StartX=-0.183722 StartY=60.6702 StartZ=0 EndX=0.183722 EndY=60.6702 EndZ=0
    g1: LineSegment StartX=-6.39707 StartY=10.7302 StartZ=0 EndX=5.82884 EndY=10.7302 EndZ=0
    g2: LineSegment StartX=-0.199998 StartY=10.9609 StartZ=0 EndX=0.2 EndY=10.961 EndZ=0
    g3: Circle CenterX=0 CenterY=16.5851 CenterZ=0 NormalX=0 NormalY=0 NormalZ=1 AngleXU=0 Radius=0.9
    g4-g7: Circle x4 (B-spline internal-alignment scaffolding for g8; pole/knot coordinates omitted)
    g8: BSplineCurve PolesCount=4 KnotsCount=2 Degree=3 IsPeriodic=0
    g9: GeomPoint X=-0.199998 Y=10.9609 Z=0
    g10: GeomPoint X=-7.83523 Y=22.1506 Z=0
    g11-g15: Circle x5 (B-spline internal-alignment scaffolding for g16; pole/knot coordinates omitted)
    g16: BSplineCurve PolesCount=5 KnotsCount=3 Degree=3 IsPeriodic=0
    g17: GeomPoint X=-0.183722 Y=60.6702 Z=0
    g18: GeomPoint X=-4.50364 Y=40.9996 Z=0
    g19: GeomPoint X=-7.83523 Y=22.1506 Z=0
    g20: BSplineCurve PolesCount=5 KnotsCount=3 Degree=3 IsPeriodic=0
    g21: BSplineCurve PolesCount=4 KnotsCount=2 Degree=3 IsPeriodic=0
  constraints (20):
    c: Weight(g4) = 1
    c: Coincident(g8,g2)
    c: Equal(g4,g5)
    c: Equal(g4,g6)
    c: Equal(g4,g7)
    c: InternalAlignment(g4-g7 -> g8) x4
    c: InternalAlignment(g9,g8)
    c: InternalAlignment(g10,g8)
    c: Symmetric(g0,g0,g-2)
    c: Weight(g11) = 1
    c: Coincident(g16,g0)
    c: Equal(g11, g12-g15) x4
    c: Coincident(g16,g8)
    c: InternalAlignment(g11-g15 -> g16) x5
    c: InternalAlignment(g17,g16)
    c: InternalAlignment(g18,g16)
    c: InternalAlignment(g19,g16)
    c: Coincident(g20,g21)
    c: Coincident(g2,g21)
    c: Coincident(g0,g20)
FEATURE [Sketcher::SketchObject] Sketch013  label="Btm Sk"
  ExternalGeometry = -> [Pocket]
  FullyConstrained = false
  Placement = pos=(760,0,142.3) rot=(0.57735,-0.57735,-0.57735;2.0944rad)
  sketch-geometry (24):
    g0: LineSegment StartX=-0.225 StartY=54.6947 StartZ=0 EndX=0.225 EndY=54.6947 EndZ=0
    g1: LineSegment StartX=-6.39707 StartY=10.7302 StartZ=0 EndX=5.82884 EndY=10.7302 EndZ=0
    g2: LineSegment StartX=-0.2 StartY=10.961 StartZ=0 EndX=0.2 EndY=10.961 EndZ=0
    g3: Circle CenterX=0 CenterY=16.5851 CenterZ=0 NormalX=0 NormalY=0 NormalZ=1 AngleXU=0 Radius=0.9
    g4-g8: Circle x5 (B-spline internal-alignment scaffolding for g9; pole/knot coordinates omitted)
    g9: BSplineCurve PolesCount=5 KnotsCount=3 Degree=3 IsPeriodic=0
    g10: GeomPoint X=-0.2 Y=10.961 Z=0
    g11: GeomPoint X=-3.5804 Y=12.8532 Z=0
    g12: GeomPoint X=-6.62316 Y=18.8138 Z=0
    g13-g17: Circle x5 (B-spline internal-alignment scaffolding for g18; pole/knot coordinates omitted)
    g18: BSplineCurve PolesCount=5 KnotsCount=3 Degree=3 IsPeriodic=0
    g19: GeomPoint X=-0.225 Y=54.6947 Z=0
    g20: GeomPoint X=-4.57012 Y=35.113 Z=0
    g21: GeomPoint X=-6.62316 Y=18.8138 Z=0
    g22: BSplineCurve PolesCount=5 KnotsCount=3 Degree=3 IsPeriodic=0
    g23: BSplineCurve PolesCount=5 KnotsCount=3 Degree=3 IsPeriodic=0
  constraints (19):
    c: Weight(g4) = 1
    c: Coincident(g9,g2)
    c: Equal(g4, g5-g8) x4
    c: InternalAlignment(g4-g8 -> g9) x5
    c: InternalAlignment(g10,g9)
    c: InternalAlignment(g11,g9)
    c: InternalAlignment(g12,g9)
    c: Symmetric(g0,g0,g-2)
    c: Weight(g13) = 1
    c: Coincident(g18,g0)
    c: Equal(g13, g14-g17) x4
    c: Coincident(g18,g9)
    c: InternalAlignment(g13-g17 -> g18) x5
    c: InternalAlignment(g19,g18)
    c: InternalAlignment(g20,g18)
    c: InternalAlignment(g21,g18)
    c: Coincident(g22,g23)
    c: Coincident(g2,g23)
    c: Coincident(g0,g22)
FEATURE [Sketcher::SketchObject] Sketch014  label="Btm Sk2"
  ExternalGeometry = -> [Pocket]
  FullyConstrained = false
  Placement = pos=(778.5,0,142.3) rot=(0.57735,-0.57735,-0.57735;2.0944rad)
  sketch-geometry (24):
    g0: LineSegment StartX=-0.271254 StartY=42.2682 StartZ=0 EndX=0.271254 EndY=42.2682 EndZ=0
    g1: LineSegment StartX=-6.39707 StartY=10.7302 StartZ=0 EndX=5.82884 EndY=10.7302 EndZ=0
    g2: LineSegment StartX=-0.2 StartY=10.961 StartZ=0 EndX=0.2 EndY=10.961 EndZ=0
    g3: Circle CenterX=0 CenterY=16.5851 CenterZ=0 NormalX=0 NormalY=0 NormalZ=1 AngleXU=0 Radius=0.9
    g4: Circle CenterX=-3.51999 CenterY=17.2962 CenterZ=0 NormalX=0 NormalY=0 NormalZ=1 AngleXU=0 Radius=1
    g5: Circle CenterX=-3.03433 CenterY=15.3419 CenterZ=0 NormalX=0 NormalY=0 NormalZ=1 AngleXU=0 Radius=1
    g6: Circle CenterX=-2.07711 CenterY=12.9545 CenterZ=0 NormalX=0 NormalY=0 NormalZ=1 AngleXU=0 Radius=1
    g7: Circle CenterX=-0.984759 CenterY=11.4792 CenterZ=0 NormalX=0 NormalY=0 NormalZ=1 AngleXU=0 Radius=1
    g8: Circle CenterX=-0.2 CenterY=10.7498 CenterZ=0 NormalX=0 NormalY=0 NormalZ=1 AngleXU=0 Radius=1
    g9: BSplineCurve PolesCount=5 KnotsCount=3 Degree=3 IsPeriodic=0
    g10: GeomPoint X=-3.51999 Y=17.2962 Z=0
    g11: GeomPoint X=-2.04333 Y=13.1825 Z=0
    g12: GeomPoint X=-0.2 Y=10.7498 Z=0
    g13: Circle CenterX=-3.51999 CenterY=17.2962 CenterZ=0 NormalX=0 NormalY=0 NormalZ=1 AngleXU=0 Radius=1
    g14: Circle CenterX=-3.08825 CenterY=22.649 CenterZ=0 NormalX=0 NormalY=0 NormalZ=1 AngleXU=0 Radius=1
    g15: Circle CenterX=-2.54219 CenterY=27.5596 CenterZ=0 NormalX=0 NormalY=0 NormalZ=1 AngleXU=0 Radius=1
    g16: Circle CenterX=-1.90148 CenterY=32.5914 CenterZ=0 NormalX=0 NormalY=0 NormalZ=1 AngleXU=0 Radius=1
    g17: Circle CenterX=-1.23651 CenterY=37.5127 CenterZ=0 NormalX=0 NormalY=0 NormalZ=1 AngleXU=0 Radius=1
    g18: BSplineCurve PolesCount=6 KnotsCount=4 Degree=3 IsPeriodic=0
    g19: GeomPoint X=-3.51999 Y=17.2962 Z=0
    g20: GeomPoint X=-2.57192 Y=27.1706 Z=0
    g21: GeomPoint X=-1.82067 Y=33.3458 Z=0
    g22: BSplineCurve PolesCount=5 KnotsCount=3 Degree=3 IsPeriodic=0
    g23: BSplineCurve PolesCount=6 KnotsCount=4 Degree=3 IsPeriodic=0
  constraints (6):
    c: Coincident(g9,g18)
    c: Coincident(g0,g18)
    c: Coincident(g2,g9)
    c: Symmetric(g0,g0,g-2)
    c: Coincident(g22,g23)
    c: Coincident(g0,g23)
FEATURE [Sketcher::SketchObject] Sketch015  label="Mid Sk01"
  ExternalGeometry = -> [Pocket]
  FullyConstrained = false
  Placement = pos=(691,0,142.3) rot=(0.57735,-0.57735,-0.57735;2.0944rad)
  sketch-geometry (29):
    g0: LineSegment StartX=-6.39707 StartY=10.7302 StartZ=0 EndX=5.82884 EndY=10.7302 EndZ=0
    g1: LineSegment StartX=-0.2 StartY=10.961 StartZ=0 EndX=0.2 EndY=10.961 EndZ=0
    g2: Circle CenterX=0 CenterY=16.5851 CenterZ=0 NormalX=0 NormalY=0 NormalZ=1 AngleXU=0 Radius=0.9
    g3: GeomPoint X=-0.2 Y=10.7498 Z=0
    g4-g9: Circle x6 (B-spline internal-alignment scaffolding for g10; pole/knot coordinates omitted)
    g10: BSplineCurve PolesCount=6 KnotsCount=4 Degree=3 IsPeriodic=0
    g11-g14: GeomPoint x4 (B-spline internal-alignment scaffolding for g10; pole/knot coordinates omitted)
    g15: LineSegment StartX=-0.244837 StartY=55.4261 StartZ=0 EndX=0.244837 EndY=55.4261 EndZ=0
    g16-g21: Circle x6 (B-spline internal-alignment scaffolding for g22; pole/knot coordinates omitted)
    g22: BSplineCurve PolesCount=6 KnotsCount=4 Degree=3 IsPeriodic=0
    g23-g26: GeomPoint x4 (B-spline internal-alignment scaffolding for g22; pole/knot coordinates omitted)
    g27: BSplineCurve PolesCount=6 KnotsCount=4 Degree=3 IsPeriodic=0
    g28: BSplineCurve PolesCount=6 KnotsCount=4 Degree=3 IsPeriodic=0
  constraints (17):
    c: Weight(g4) = 1
    c: Equal(g4, g5-g9) x5
    c: InternalAlignment(g4-g9 -> g10) x6
    c: InternalAlignment(g11-g14 -> g10) x4
    c: Coincident(g15,g10)
    c: Symmetric(g10,g15,g-2)
    c: Symmetric(g1,g1,g-2)
    c: DistanceX(g1,g1) = 0.4
    c: Weight(g16) = 1
    c: Coincident(g22,g10)
    c: Equal(g16, g17-g21) x5
    c: Coincident(g22,g1)
    c: InternalAlignment(g16-g21 -> g22) x6
    c: InternalAlignment(g23-g26 -> g22) x4
    c: Coincident(g27,g28)
    c: Coincident(g1,g28)
    c: Coincident(g15,g27)
FEATURE [PartDesign::AdditiveLoft] AdditiveLoft001
  Closed = false
  Placement = pos=(657.694,9e-14,142.303) rot=(-0.57735,0.57735,0.57735;4.18879rad)
  Profile = -> Sketch009
  Ruled = false
  Sections = -> [Sketch011,Sketch015,Sketch010,Sketch012,Sketch013,Sketch014]
FEATURE [PartDesign::ShapeBinder] ShapeBinder
  Support = -> [Pocket]
  TraceSupport = false
FEATURE [Sketcher::SketchObject] Sketch016  label="SubLft1"
  AttachmentOffset = pos=(0,0,142) rot=(0,0,1;0rad)
  ExternalGeometry = -> [ShapeBinder]
  FullyConstrained = false
  MapMode = 5
  Placement = pos=(0,0,142) rot=(0,0,1;0rad)
  Support = -> [XY_Plane002]
  sketch-geometry (28):
    g0: LineSegment StartX=780.046 StartY=0.25 StartZ=0 EndX=780.046 EndY=-0.255842 EndZ=0
    g1-g6: Circle x6 (B-spline internal-alignment scaffolding for g7; pole/knot coordinates omitted)
    g7: BSplineCurve PolesCount=6 KnotsCount=4 Degree=3 IsPeriodic=0
    g8-g11: GeomPoint x4 (B-spline internal-alignment scaffolding for g7; pole/knot coordinates omitted)
    g12-g17: Circle x6 (B-spline internal-alignment scaffolding for g18; pole/knot coordinates omitted)
    g18: BSplineCurve PolesCount=6 KnotsCount=4 Degree=3 IsPeriodic=0
    g19-g22: GeomPoint x4 (B-spline internal-alignment scaffolding for g18; pole/knot coordinates omitted)
    g23: LineSegment StartX=759.191 StartY=9.43465 StartZ=0 EndX=759.191 EndY=27.4666 EndZ=0
    g24: LineSegment StartX=759.191 StartY=27.4666 StartZ=0 EndX=799.809 EndY=27.4666 EndZ=0
    g25: LineSegment StartX=799.809 StartY=27.4666 StartZ=0 EndX=799.809 EndY=-25.4455 EndZ=0
    g26: LineSegment StartX=799.809 StartY=-25.4455 StartZ=0 EndX=759.253 EndY=-25.4455 EndZ=0
    g27: LineSegment StartX=759.253 StartY=-25.4455 StartZ=0 EndX=759.253 EndY=-9.45272 EndZ=0
  constraints (28):
    c: Coincident(g0,g-3)
    c: Coincident(g0,g-4)
    c: Weight(g1) = 1
    c: Coincident(g7,g0)
    c: Equal(g1, g2-g6) x5
    c: InternalAlignment(g1-g6 -> g7) x6
    c: InternalAlignment(g8-g11 -> g7) x4
    c: Weight(g12) = 1
    c: Coincident(g18,g0)
    c: Equal(g12, g13-g17) x5
    c: Coincident(g18,g-4)
    c: InternalAlignment(g12-g17 -> g18) x6
    c: InternalAlignment(g19-g22 -> g18) x4
    c: Symmetric(g16,g5,g-1)
    c: Symmetric(g4,g15,g-1)
    c: Symmetric(g3,g14,g-1)
    c: Symmetric(g13,g2,g-1)
    c: Coincident(g23,g7)
    c: Vertical(g23)
    c: Coincident(g23,g24)
    c: Horizontal(g24)
    c: Coincident(g24,g25)
    c: Vertical(g25)
    c: Coincident(g25,g26)
    c: Horizontal(g26)
    c: Coincident(g26,g27)
    c: Coincident(g27,g18)
    c: Vertical(g27)
FEATURE [PartDesign::SubtractiveLoft] SubtractiveLoft001
  BaseFeature = -> AdditiveLoft001
  Closed = false
  Placement = pos=(657.694,9e-14,142.303) rot=(-0.57735,0.57735,0.57735;4.18879rad)
  Profile = -> Sketch016
  Ruled = false
  Sections = -> [Sketch017,Sketch018]
FEATURE [PartDesign::ShapeBinder] ShapeBinder001
  Support = -> [Pocket]
  TraceSupport = false
FEATURE [Sketcher::SketchObject] Sketch019
  ExternalGeometry = -> [ShapeBinder001]
  FullyConstrained = false
  MapMode = 5
  Placement = pos=(0,0,0) rot=(1,0,0;1.5708rad)
  Support = -> [XZ_Plane002]
  sketch-geometry (12):
    g0: LineSegment StartX=725.616 StartY=151.912 StartZ=0 EndX=725.616 EndY=162.912 EndZ=0
    g1: LineSegment StartX=725.616 StartY=162.912 StartZ=0 EndX=737.552 EndY=162.912 EndZ=0
    g2: LineSegment StartX=737.552 StartY=162.912 StartZ=0 EndX=737.552 EndY=152.444 EndZ=0
    g3: LineSegment StartX=737.552 StartY=152.444 StartZ=0 EndX=766.862 EndY=152.444 EndZ=0
    g4: LineSegment StartX=766.862 StartY=152.444 StartZ=0 EndX=766.862 EndY=162.912 EndZ=0
    g5: LineSegment StartX=766.862 StartY=162.912 StartZ=0 EndX=779.409 EndY=162.912 EndZ=0
    g6: LineSegment StartX=779.409 StartY=162.912 StartZ=0 EndX=779.409 EndY=149.239 EndZ=0
    g7: LineSegment StartX=669.99 StartY=151.912 StartZ=0 EndX=669.99 EndY=162.912 EndZ=0
    g8: LineSegment StartX=669.99 StartY=162.912 StartZ=0 EndX=648.709 EndY=162.912 EndZ=0
    g9: LineSegment StartX=648.709 StartY=162.912 StartZ=0 EndX=648.709 EndY=149.239 EndZ=0
    g10: LineSegment StartX=725.616 StartY=151.912 StartZ=0 EndX=669.99 EndY=151.912 EndZ=0
    g11: LineSegment StartX=648.709 StartY=149.239 StartZ=0 EndX=779.409 EndY=149.239 EndZ=0
  constraints (32):
    c: Vertical(g0)
    c: Coincident(g0,g1)
    c: Horizontal(g1)
    c: Coincident(g1,g2)
    c: Vertical(g2)
    c: Coincident(g2,g3)
    c: Horizontal(g3)
    c: Coincident(g3,g4)
    c: Coincident(g4,g5)
    c: Horizontal(g5)
    c: Coincident(g5,g6)
    c: Vertical(g6)
    c: Vertical(g7)
    c: Coincident(g7,g8)
    c: Horizontal(g8)
    c: Coincident(g8,g9)
    c: Vertical(g9)
    c: Coincident(g10,g0)
    c: Horizontal(g10)
    c: Coincident(g7,g10)
    c: Coincident(g11,g9)
    c: Coincident(g11,g6)
    c: Horizontal(g11)
    c: DistanceX(g-4,g7) = 0.5
    c: DistanceX(g0,g-4) = 0.5
    c: DistanceX(g-3,g2) = 0.5
    c: Vertical(g4)
    c: DistanceX(g3,g-3) = 0.5
    c: Horizontal(g4,g1)
    c: Horizontal(g1,g7)
    c: DistanceY(g7,g7) = 11  'Heightcut'
    c: DistanceY(g7,g-4) = 1
FEATURE [PartDesign::Pocket] Pocket001
  BaseFeature = -> SubtractiveLoft001
  Direction = (0,1,2e-16)
  Length = 5
  Length2 = 5
  Midplane = true
  Placement = pos=(657.694,9e-14,142.303) rot=(-0.57735,0.57735,0.57735;4.18879rad)
  Profile = -> Sketch019
  ReferenceAxis = -> Sketch019 [N_Axis]
  Type = 1
FEATURE [PartDesign::ShapeBinder] ShapeBinder002
  Placement = pos=(657.694,9e-14,142.303) rot=(-0.57735,0.57735,0.57735;4.18879rad)
  Support = -> [Pocket001]
  TraceSupport = false
FEATURE [PartDesign::ShapeBinder] ShapeBinder003
  Support = -> [Pocket]
  TraceSupport = false
FEATURE [Sketcher::SketchObject] Sketch020  label="BaseSk"
  ExternalGeometry = -> [ShapeBinder002,ShapeBinder003]
  FullyConstrained = true
  MapMode = 5
  Placement = pos=(657.694,9e-14,142.303) rot=(-0.57735,0.57735,0.57735;4.18879rad)
  Support = -> [ShapeBinder002]
  sketch-geometry (6):
    g0: ArcOfCircle CenterX=0 CenterY=3.8 CenterZ=0 NormalX=0 NormalY=0 NormalZ=1 AngleXU=0 Radius=4 StartAngle=3.26692 EndAngle=6.15786
    g1: ArcOfCircle CenterX=176.028 CenterY=4.40754 CenterZ=0 NormalX=0 NormalY=0 NormalZ=1 AngleXU=0 Radius=180 StartAngle=3.05146 EndAngle=3.14775
    g2: ArcOfCircle CenterX=-176.028 CenterY=4.40754 CenterZ=0 NormalX=0 NormalY=0 NormalZ=1 AngleXU=0 Radius=180 StartAngle=6.27703 EndAngle=6.37331
    g3: LineSegment StartX=-3.24144 StartY=20.6088 StartZ=0 EndX=-0.225 EndY=47.2182 EndZ=0
    g4: LineSegment StartX=-0.225 StartY=47.2182 StartZ=0 EndX=0.225 EndY=47.2182 EndZ=0
    g5: LineSegment StartX=0.225 StartY=47.2182 StartZ=0 EndX=3.24144 EndY=20.6088 EndZ=0
  constraints (17):
    c: PointOnObject(g0,g-2)
    c: Horizontal(g0,g0)
    c: Radius(g0) = 4
    c: DistanceY(g0,g0) = 0.5
    c: DistanceY(g-5,g0) = 4.2
    c: Coincident(g1,g0)
    c: Coincident(g1,g-3)
    c: Radius(g1) = 180
    c: Coincident(g2,g-3)
    c: Coincident(g2,g0)
    c: Radius(g2) = 180
    c: Coincident(g1,g3)
    c: Coincident(g3,g-4)
    c: Coincident(g3,g4)
    c: Coincident(g4,g-4)
    c: Coincident(g4,g5)
    c: Coincident(g5,g2)
FEATURE [Sketcher::SketchObject] Sketch021  label="BaseSk001"
  AttachmentOffset = pos=(0,0,9) rot=(0,0,1;0rad)
  ExternalGeometry = -> [ShapeBinder003]
  FullyConstrained = false
  MapMode = 5
  Placement = pos=(648.694,9e-14,142.303) rot=(-0.57735,0.57735,0.57735;4.18879rad)
  Support = -> [ShapeBinder002]
  sketch-geometry (6):
    g0: ArcOfCircle CenterX=0 CenterY=3.8 CenterZ=0 NormalX=0 NormalY=0 NormalZ=1 AngleXU=0 Radius=4 StartAngle=3.26692 EndAngle=6.15786
    g1: LineSegment StartX=-0.24 StartY=40.6005 StartZ=0 EndX=0.24 EndY=40.6005 EndZ=0
    g2: LineSegment StartX=-0.24 StartY=40.6005 StartZ=0 EndX=-3.125 EndY=15.8997 EndZ=0
    g3: LineSegment StartX=3.125 StartY=15.8997 StartZ=0 EndX=0.24 EndY=40.6005 EndZ=0
    g4: ArcOfCircle CenterX=96.0307 CenterY=2.93256 CenterZ=0 NormalX=0 NormalY=0 NormalZ=1 AngleXU=0 Radius=100 StartAngle=3.01155 EndAngle=3.13792
    g5: ArcOfCircle CenterX=-96.0307 CenterY=2.93256 CenterZ=0 NormalX=0 NormalY=0 NormalZ=1 AngleXU=0 Radius=100 StartAngle=0.00367446 EndAngle=0.130038
  constraints (17):
    c: PointOnObject(g0,g-2)
    c: Horizontal(g0,g0)
    c: Radius(g0) = 4
    c: DistanceY(g0,g0) = 0.5
    c: DistanceY(g-3,g0) = 4.2
    c: Symmetric(g2,g3,g-2)
    c: Symmetric(g1,g1,g-2)
    c: DistanceX(g1,g1) = 0.48
    c: Coincident(g2,g1)
    c: DistanceX(g2,g3) = 6.25
    c: Coincident(g3,g1)
    c: Coincident(g4,g0)
    c: Radius(g4) = 100
    c: Coincident(g5,g0)
    c: Radius(g5) = 100
    c: Coincident(g3,g5)
    c: Coincident(g2,g4)
FEATURE [Sketcher::SketchObject] Sketch022  label="BaseSk002"
  AttachmentOffset = pos=(0,0,17) rot=(0,0,1;0rad)
  ExternalGeometry = -> [ShapeBinder003]
  FullyConstrained = false
  MapMode = 5
  Placement = pos=(640.694,9e-14,142.303) rot=(-0.57735,0.57735,0.57735;4.18879rad)
  Support = -> [ShapeBinder002]
  sketch-geometry (6):
    g0: ArcOfCircle CenterX=0 CenterY=2.8 CenterZ=0 NormalX=0 NormalY=0 NormalZ=1 AngleXU=0 Radius=3 StartAngle=3.30904 EndAngle=6.11574
    g1: LineSegment StartX=3.30188 StartY=10.7731 StartZ=0 EndX=0.225 EndY=29.9571 EndZ=0
    g2: LineSegment StartX=-0.225 StartY=29.9571 StartZ=0 EndX=-3.30188 EndY=10.7731 EndZ=0
    g3: LineSegment StartX=-0.225 StartY=29.9571 StartZ=0 EndX=0.225 EndY=29.9571 EndZ=0
    g4: ArcOfCircle CenterX=21.4876 CenterY=7.53554 CenterZ=0 NormalX=0 NormalY=0 NormalZ=1 AngleXU=0 Radius=25 StartAngle=3.01172 EndAngle=3.35258
    g5: ArcOfCircle CenterX=-21.4876 CenterY=7.53554 CenterZ=0 NormalX=0 NormalY=0 NormalZ=1 AngleXU=0 Radius=25 StartAngle=6.0722 EndAngle=6.41305
  constraints (16):
    c: PointOnObject(g0,g-2)
    c: Horizontal(g0,g0)
    c: Radius(g0) = 3
    c: DistanceY(g0,g0) = 0.5
    c: DistanceY(g-3,g0) = 3.2
    c: Symmetric(g3,g3,g-2)
    c: DistanceX(g3,g3) = 0.45
    c: Symmetric(g2,g1,g-2)
    c: Coincident(g2,g3)
    c: Coincident(g1,g3)
    c: Coincident(g4,g2)
    c: Coincident(g4,g0)
    c: Radius(g4) = 25
    c: Coincident(g5,g1)
    c: Coincident(g5,g0)
    c: Radius(g5) = 25
FEATURE [Sketcher::SketchObject] Sketch023  label="BaseSk003"
  AttachmentOffset = pos=(0,0,25) rot=(0,0,1;0rad)
  ExternalGeometry = -> [ShapeBinder003]
  FullyConstrained = false
  MapMode = 5
  Placement = pos=(632.694,9e-14,142.303) rot=(-0.57735,0.57735,0.57735;4.18879rad)
  Support = -> [ShapeBinder002]
  sketch-geometry (6):
    g0: ArcOfCircle CenterX=0 CenterY=2.1 CenterZ=0 NormalX=0 NormalY=0 NormalZ=1 AngleXU=0 Radius=2.26972 StartAngle=3.94573 EndAngle=5.47904
    g1: LineSegment StartX=-1.74021 StartY=2.95145 StartZ=0 EndX=-0.339202 EndY=8.91755 EndZ=0
    g2: LineSegment StartX=0.339202 StartY=8.91755 StartZ=0 EndX=1.74021 EndY=2.95145 EndZ=0
    g3: LineSegment StartX=-0.339202 StartY=8.91755 StartZ=0 EndX=0.339202 EndY=8.91755 EndZ=0
    g4: ArcOfCircle CenterX=35.0365 CenterY=4.15296 CenterZ=0 NormalX=0 NormalY=0 NormalZ=1 AngleXU=0 Radius=36.7963 StartAngle=3.17425 EndAngle=3.24198
    g5: ArcOfCircle CenterX=-26.6467 CenterY=3.59402 CenterZ=0 NormalX=0 NormalY=0 NormalZ=1 AngleXU=0 Radius=28.3942 StartAngle=6.17277 EndAngle=6.26055
  constraints (11):
    c: PointOnObject(g0,g-2)
    c: Horizontal(g0,g0)
    c: Symmetric(g1,g2,g-2)
    c: Symmetric(g1,g2,g-2)
    c: Coincident(g3,g1)
    c: Coincident(g3,g2)
    c: DistanceY(g-3,g0) = 2.5
    c: Coincident(g4,g0)
    c: Coincident(g4,g1)
    c: Coincident(g5,g0)
    c: Coincident(g5,g2)
FEATURE [PartDesign::AdditiveLoft] AdditiveLoft002
  Closed = false
  Placement = pos=(657.694,9e-14,142.303) rot=(-0.57735,0.57735,0.57735;4.18879rad)
  Profile = -> Sketch020
  Ruled = false
  Sections = -> [Sketch021,Sketch022,Sketch023]
FEATURE [PartDesign::Plane] DatumPlane002
  AttachmentOffset = pos=(0,0,140) rot=(0,0,1;0rad)
  Length = 719.645
  MapMode = 5
  Placement = pos=(0,0,140) rot=(0,0,1;0rad)
  ResizeMode = 0
  Support = -> [XY_Plane003]
  Width = 86.9511
FEATURE [PartDesign::Plane] DatumPlane003
  AttachmentOffset = pos=(0,0,153) rot=(0,0,1;0rad)
  Length = 719.645
  MapMode = 5
  Placement = pos=(0,0,153) rot=(0,0,1;0rad)
  ResizeMode = 0
  Support = -> [XY_Plane003]
  Width = 86.9511
FEATURE [PartDesign::Plane] DatumPlane004
  AttachmentOffset = pos=(0,0,175) rot=(0,0,1;0rad)
  Length = 719.645
  MapMode = 5
  Placement = pos=(0,0,175) rot=(0,0,1;0rad)
  ResizeMode = 0
  Support = -> [XY_Plane003]
  Width = 86.9511
FEATURE [Sketcher::SketchObject] Sketch024
  FullyConstrained = false
  MapMode = 5
  Placement = pos=(0,0,140) rot=(0,0,1;0rad)
  Support = -> [DatumPlane002]
  sketch-geometry (26):
    g0-g6: Circle x7 (B-spline internal-alignment scaffolding for g7; pole/knot coordinates omitted)
    g7: BSplineCurve PolesCount=11 KnotsCount=9 Degree=3 IsPeriodic=0
    g8-g16: GeomPoint x9 (B-spline internal-alignment scaffolding for g7; pole/knot coordinates omitted)
    g17-g20: Circle x4 (B-spline internal-alignment scaffolding for g7; pole/knot coordinates omitted)
    g21: LineSegment StartX=657.982 StartY=5.15473 StartZ=0 EndX=657.982 EndY=14.1163 EndZ=0
    g22: LineSegment StartX=657.982 StartY=14.1163 StartZ=0 EndX=625.728 EndY=14.1163 EndZ=0
    g23: LineSegment StartX=625.728 StartY=14.1163 StartZ=0 EndX=625.728 EndY=-12.7421 EndZ=0
    g24: LineSegment StartX=625.728 StartY=-12.7421 StartZ=0 EndX=657.982 EndY=-12.7421 EndZ=0
    g25: LineSegment StartX=657.982 StartY=-12.7421 StartZ=0 EndX=657.982 EndY=-5.15473 EndZ=0
  constraints (29):
    c: Weight(g0) = 1
    c: Equal(g0, g1-g6) x6
    c: InternalAlignment(g0-g6 -> g7) x7
    c: InternalAlignment(g8-g17 -> g7) x10
    c: Equal(g17,g0)
    c: InternalAlignment(g18,g7)
    c: Equal(g18,g0)
    c: Symmetric(g7,g7,g-1)
    c: Symmetric(g18,g1,g-1)
    c: Symmetric(g17,g2,g-1)
    c: Symmetric(g3,g5,g-1)
    c: InternalAlignment(g19,g7)
    c: Equal(g19,g0)
    c: InternalAlignment(g20,g7)
    c: Equal(g20,g0)
    c: Symmetric(g4,g19,g-1)
    c: DistanceX(g7) = 657.982
    c: DistanceY(g7) = 5.15473
    c: Coincident(g21,g7)
    c: Vertical(g21)
    c: Coincident(g21,g22)
    c: Horizontal(g22)
    c: Coincident(g22,g23)
    c: Vertical(g23)
    c: Coincident(g23,g24)
    c: Horizontal(g24)
    c: Coincident(g24,g25)
    c: Coincident(g25,g7)
    c: Vertical(g25)
FEATURE [Sketcher::SketchObject] Sketch025
  FullyConstrained = false
  MapMode = 5
  Placement = pos=(0,0,153) rot=(0,0,1;0rad)
  Support = -> [DatumPlane003]
  sketch-geometry (26):
    g0-g6: Circle x7 (B-spline internal-alignment scaffolding for g7; pole/knot coordinates omitted)
    g7: BSplineCurve PolesCount=11 KnotsCount=9 Degree=3 IsPeriodic=0
    g8-g16: GeomPoint x9 (B-spline internal-alignment scaffolding for g7; pole/knot coordinates omitted)
    g17-g20: Circle x4 (B-spline internal-alignment scaffolding for g7; pole/knot coordinates omitted)
    g21: LineSegment StartX=657.982 StartY=4.11084 StartZ=0 EndX=657.982 EndY=14.1163 EndZ=0
    g22: LineSegment StartX=657.982 StartY=14.1163 StartZ=0 EndX=625.728 EndY=14.1163 EndZ=0
    g23: LineSegment StartX=625.728 StartY=14.1163 StartZ=0 EndX=625.728 EndY=-12.7421 EndZ=0
    g24: LineSegment StartX=625.728 StartY=-12.7421 StartZ=0 EndX=657.982 EndY=-12.7421 EndZ=0
    g25: LineSegment StartX=657.982 StartY=-12.7421 StartZ=0 EndX=657.982 EndY=-4.11084 EndZ=0
  constraints (28):
    c: Weight(g0) = 1
    c: Equal(g0, g1-g6) x6
    c: InternalAlignment(g0-g6 -> g7) x7
    c: InternalAlignment(g8-g17 -> g7) x10
    c: Equal(g17,g0)
    c: InternalAlignment(g18,g7)
    c: Equal(g18,g0)
    c: Symmetric(g7,g7,g-1)
    c: Symmetric(g18,g1,g-1)
    c: Symmetric(g17,g2,g-1)
    c: Symmetric(g3,g5,g-1)
    c: InternalAlignment(g19,g7)
    c: Equal(g19,g0)
    c: InternalAlignment(g20,g7)
    c: Equal(g20,g0)
    c: Symmetric(g4,g19,g-1)
    c: DistanceX(g7) = 657.982
    c: Coincident(g21,g7)
    c: Vertical(g21)
    c: Coincident(g21,g22)
    c: Horizontal(g22)
    c: Coincident(g22,g23)
    c: Vertical(g23)
    c: Coincident(g23,g24)
    c: Horizontal(g24)
    c: Coincident(g24,g25)
    c: Coincident(g25,g7)
    c: Vertical(g25)
FEATURE [Sketcher::SketchObject] Sketch026
  FullyConstrained = false
  MapMode = 5
  Placement = pos=(0,0,175) rot=(0,0,1;0rad)
  Support = -> [DatumPlane004]
  sketch-geometry (26):
    g0-g6: Circle x7 (B-spline internal-alignment scaffolding for g7; pole/knot coordinates omitted)
    g7: BSplineCurve PolesCount=11 KnotsCount=9 Degree=3 IsPeriodic=0
    g8-g16: GeomPoint x9 (B-spline internal-alignment scaffolding for g7; pole/knot coordinates omitted)
    g17-g20: Circle x4 (B-spline internal-alignment scaffolding for g7; pole/knot coordinates omitted)
    g21: LineSegment StartX=657.982 StartY=2.05135 StartZ=0 EndX=657.982 EndY=14.1163 EndZ=0
    g22: LineSegment StartX=657.982 StartY=14.1163 StartZ=0 EndX=625.728 EndY=14.1163 EndZ=0
    g23: LineSegment StartX=625.728 StartY=14.1163 StartZ=0 EndX=625.728 EndY=-12.7421 EndZ=0
    g24: LineSegment StartX=625.728 StartY=-12.7421 StartZ=0 EndX=657.982 EndY=-12.7421 EndZ=0
    g25: LineSegment StartX=657.982 StartY=-12.7421 StartZ=0 EndX=657.982 EndY=-2.05135 EndZ=0
  constraints (28):
    c: Weight(g0) = 1
    c: Equal(g0, g1-g6) x6
    c: InternalAlignment(g0-g6 -> g7) x7
    c: InternalAlignment(g8-g17 -> g7) x10
    c: Equal(g17,g0)
    c: InternalAlignment(g18,g7)
    c: Equal(g18,g0)
    c: Symmetric(g7,g7,g-1)
    c: Symmetric(g18,g1,g-1)
    c: Symmetric(g17,g2,g-1)
    c: Symmetric(g3,g5,g-1)
    c: InternalAlignment(g19,g7)
    c: Equal(g19,g0)
    c: InternalAlignment(g20,g7)
    c: Equal(g20,g0)
    c: Symmetric(g4,g19,g-1)
    c: DistanceX(g7) = 657.982
    c: Coincident(g21,g7)
    c: Vertical(g21)
    c: Coincident(g21,g22)
    c: Horizontal(g22)
    c: Coincident(g22,g23)
    c: Vertical(g23)
    c: Coincident(g23,g24)
    c: Horizontal(g24)
    c: Coincident(g24,g25)
    c: Coincident(g25,g7)
    c: Vertical(g25)
FEATURE [PartDesign::SubtractiveLoft] SubtractiveLoft002
  BaseFeature = -> AdditiveLoft002
  Closed = false
  Placement = pos=(657.694,9e-14,142.303) rot=(-0.57735,0.57735,0.57735;4.18879rad)
  Profile = -> Sketch024
  Ruled = false
  Sections = -> [Sketch025,Sketch026]
FEATURE [Sketcher::SketchObject] Sketch027
  FullyConstrained = false
  MapMode = 5
  Placement = pos=(657.694,9e-14,142.303) rot=(-0.57735,0.57735,-0.57735;2.0944rad)
  Support = -> [SubtractiveLoft002]
  sketch-geometry (4):
    g0: LineSegment StartX=-7.12443 StartY=3.02241 StartZ=0 EndX=7.24063 EndY=3.02241 EndZ=0
    g1: LineSegment StartX=7.24063 StartY=3.02241 StartZ=0 EndX=7.24063 EndY=-20.6431 EndZ=0
    g2: LineSegment StartX=7.24063 StartY=-20.6431 StartZ=0 EndX=-7.12443 EndY=-20.6431 EndZ=0
    g3: LineSegment StartX=-7.12443 StartY=-20.6431 StartZ=0 EndX=-7.12443 EndY=3.02241 EndZ=0
  constraints (8):
    c: Coincident(g0,g1)
    c: Coincident(g1,g2)
    c: Coincident(g2,g3)
    c: Coincident(g3,g0)
    c: Horizontal(g0)
    c: Horizontal(g2)
    c: Vertical(g1)
    c: Vertical(g3)
FEATURE [PartDesign::Pocket] Pocket002
  BaseFeature = -> SubtractiveLoft002
  Direction = (-1,-4e-16,4e-16)
  Length = 0.5
  Length2 = 5
  Placement = pos=(657.694,9e-14,142.303) rot=(-0.57735,0.57735,0.57735;4.18879rad)
  Profile = -> Sketch027
  ReferenceAxis = -> Sketch027 [N_Axis]
  Type = 0
FEATURE [PartDesign::Body] Body003  label="TopRudder"
  Group = -> [ShapeBinder002,ShapeBinder003,Sketch020,Sketch021,Sketch022,Sketch023,AdditiveLoft002,DatumPlane002,DatumPlane003,DatumPlane004,Sketch024,Sketch025,Sketch026,SubtractiveLoft002,Sketch027,Pocket002]
  Origin = -> Origin003
  Tip = -> Pocket002
FEATURE [PartDesign::Plane] DatumPlane005
  Length = 74.9852
  MapMode = 5
  Placement = pos=(737.552,1.077e-13,142.303) rot=(0.57735,-0.57735,-0.57735;2.0944rad)
  ResizeMode = 0
  Support = -> [Pocket001]
  Width = 249.982
FEATURE [Sketcher::SketchObject] Sketch028  label="HornSk"
  AttachmentOffset = pos=(0,0,-29.3) rot=(0,0,1;0rad)
  FullyConstrained = false
  MapMode = 5
  Placement = pos=(766.852,1.142e-13,142.303) rot=(0.57735,-0.57735,-0.57735;2.0944rad)
  Support = -> [DatumPlane005]
  sketch-geometry (8):
    g0: LineSegment StartX=25 StartY=16.6 StartZ=0 EndX=0 EndY=16.6 EndZ=0
    g1: LineSegment StartX=-1.43943 StartY=26.8165 StartZ=0 EndX=-1.43943 EndY=12.7654 EndZ=0
    g2: ArcOfCircle CenterX=-0.986879 CenterY=-19.7305 CenterZ=0 NormalX=0 NormalY=0 NormalZ=1 AngleXU=0 Radius=46.5493 StartAngle=1.58052 EndAngle=2.15484
    g3: ArcOfCircle CenterX=-7.16243 CenterY=187.508 CenterZ=0 NormalX=0 NormalY=0 NormalZ=1 AngleXU=0 Radius=174.837 StartAngle=4.6084 EndAngle=4.6999
    g4: ArcOfCircle CenterX=-25 CenterY=16.6 CenterZ=0 NormalX=0 NormalY=0 NormalZ=1 AngleXU=0 Radius=3 StartAngle=2.15484 EndAngle=4.6084
    g5: Circle CenterX=-25 CenterY=16.6 CenterZ=0 NormalX=0 NormalY=0 NormalZ=1 AngleXU=0 Radius=0.6
    g6: ArcOfCircle CenterX=-6.76914 CenterY=12.6233 CenterZ=0 NormalX=0 NormalY=0 NormalZ=1 AngleXU=0 Radius=2.57827 StartAngle=0.0285638 EndAngle=3.11753
    g7: ArcOfCircle CenterX=-7.16243 CenterY=187.508 CenterZ=0 NormalX=0 NormalY=0 NormalZ=1 AngleXU=0 Radius=174.837 StartAngle=4.72938 EndAngle=4.74513
  constraints (15):
    c: PointOnObject(g0,g-2)
    c: Horizontal(g0)
    c: DistanceX(g0,g0) = 25
    c: DistanceY(g-1,g0) = 16.6
    c: Diameter(g5) = 1.2
    c: Coincident(g4,g5)
    c: Diameter(g4) = 6
    c: Coincident(g1,g2)
    c: Coincident(g1,g7)
    c: Tangent(g2,g4) = -1.5708
    c: Tangent(g3,g4) = -1.5708
    c: Equal(g3,g7)
    c: Coincident(g3,g6)
    c: Coincident(g7,g6)
    c: Coincident(g3,g7)
FEATURE [PartDesign::Pad] Pad001
  BaseFeature = -> Pocket001
  Direction = (-1,-2e-16,2e-16)
  Length = 0.75
  Length2 = 10
  Placement = pos=(657.694,9e-14,142.303) rot=(-0.57735,0.57735,0.57735;4.18879rad)
  Profile = -> Sketch028
  ReferenceAxis = -> Sketch028 [N_Axis]
  Type = 0
FEATURE [Sketcher::SketchObject] Sketch029
  FullyConstrained = false
  MapMode = 5
  Placement = pos=(0,0,0) rot=(1,0,0;1.5708rad)
  Support = -> [XZ_Plane006]
  sketch-geometry (18):
    g0: LineSegment StartX=657.37 StartY=192.111 StartZ=0 EndX=657.67 EndY=192.111 EndZ=0
    g1: LineSegment StartX=657.67 StartY=192.111 StartZ=0 EndX=657.67 EndY=154.694 EndZ=0
    g2: LineSegment StartX=657.67 StartY=154.694 StartZ=0 EndX=657.37 EndY=154.694 EndZ=0
    g3: LineSegment StartX=657.37 StartY=154.694 StartZ=0 EndX=657.37 EndY=158.091 EndZ=0
    g4: LineSegment StartX=635.069 StartY=190.59 StartZ=0 EndX=657.37 EndY=171.877 EndZ=0
    g5: LineSegment StartX=635.664 StartY=189.569 StartZ=0 EndX=635.069 EndY=190.59 EndZ=0
    g6: LineSegment StartX=633.171 StartY=157.543 StartZ=0 EndX=657.257 EndY=171.45 EndZ=0
    g7: LineSegment StartX=632.305 StartY=156.582 StartZ=0 EndX=633.171 EndY=157.543 EndZ=0
    g8: LineSegment StartX=630.682 StartY=143.145 StartZ=0 EndX=657.37 EndY=158.553 EndZ=0
    g9: LineSegment StartX=657.37 StartY=158.091 StartZ=0 EndX=630.493 EndY=142.574 EndZ=0
    g10: LineSegment StartX=630.493 StartY=142.574 StartZ=0 EndX=630.682 EndY=143.145 EndZ=0
    g11: LineSegment StartX=657.37 StartY=171.053 StartZ=0 EndX=632.305 EndY=156.582 EndZ=0
    g12: LineSegment StartX=657.257 StartY=171.45 StartZ=0 EndX=635.664 EndY=189.569 EndZ=0
    g13: LineSegment StartX=647.349 StartY=179.764 StartZ=0 EndX=647.606 EndY=180.071 EndZ=0
    g14: LineSegment StartX=649.919 StartY=167.213 StartZ=0 EndX=650.119 EndY=166.866 EndZ=0
    g15: LineSegment StartX=657.37 StartY=171.877 StartZ=0 EndX=657.37 EndY=192.111 EndZ=0
    g16: LineSegment StartX=649.977 StartY=154.285 StartZ=0 EndX=650.177 EndY=153.938 EndZ=0
    g17: LineSegment StartX=657.37 StartY=158.553 StartZ=0 EndX=657.37 EndY=171.053 EndZ=0
  constraints (42):
    c: Coincident(g0,g1)
    c: Coincident(g1,g2)
    c: Coincident(g2,g3)
    c: Coincident(g15,g0)
    c: Horizontal(g0)
    c: Horizontal(g2)
    c: Vertical(g1)
    c: Vertical(g3)
    c: Coincident(g12,g5)
    c: Coincident(g5,g4)
    c: Coincident(g11,g7)
    c: Coincident(g7,g6)
    c: Coincident(g9,g10)
    c: Coincident(g10,g8)
    c: DistanceX(g0,g0) = 0.3
    c: Coincident(g12,g6)
    c: DistanceX(g1) = 657.67
    c: DistanceY(g1) = 154.694
    c: Angle(g3,g4) = 0.872665
    c: Parallel(g12,g4)
    c: Angle(g3,g11) = 2.0944
    c: PointOnObject(g13,g12)
    c: PointOnObject(g13,g4)
    c: Perpendicular(g4,g13)
    c: Distance(g13) = 0.4
    c: Parallel(g6,g11)
    c: PointOnObject(g14,g6)
    c: PointOnObject(g14,g11)
    c: Perpendicular(g11,g14)
    c: Distance(g14) = 0.4
    c: Coincident(g17,g11)
    c: Coincident(g15,g4)
    c: Parallel(g11,g8)
    c: Parallel(g8,g9)
    c: Vertical(g17,g4)
    c: Vertical(g15)
    c: PointOnObject(g16,g8)
    c: PointOnObject(g16,g9)
    c: Perpendicular(g8,g16)
    c: Distance(g16) = 0.4
    c: Coincident(g3,g9)
    c: Coincident(g17,g8)
FEATURE [PartDesign::Pad] Pad002
  Direction = (0,-1,-2e-16)
  Length = 10
  Length2 = 10
  Midplane = true
  Placement = pos=(0,0,0) rot=(1,0,0;1.5708rad)
  Profile = -> Sketch029
  ReferenceAxis = -> Sketch029 [N_Axis]
  Type = 0
FEATURE [PartDesign::Body] Body004  label="Struct top rudder"
  Group = -> [Sketch029,Pad002]
  Origin = -> Origin006
  Tip = -> Pad002
FEATURE [Sketcher::SketchObject] Sketch030
  FullyConstrained = false
  MapMode = 5
  Placement = pos=(0,0,0) rot=(1,0,0;1.5708rad)
  Support = -> [XZ_Plane007]
  sketch-geometry (20):
    g0: LineSegment StartX=657.584 StartY=196.876 StartZ=0 EndX=657.884 EndY=196.876 EndZ=0
    g1: LineSegment StartX=657.884 StartY=196.876 StartZ=0 EndX=657.884 EndY=190.718 EndZ=0
    g2: LineSegment StartX=657.884 StartY=161.636 StartZ=0 EndX=657.584 EndY=161.636 EndZ=0
    g3: LineSegment StartX=657.584 StartY=161.636 StartZ=0 EndX=657.584 EndY=196.876 EndZ=0
    g4: LineSegment StartX=769.434 StartY=199.089 StartZ=0 EndX=769.434 EndY=198.67 EndZ=0
    g5: LineSegment StartX=769.434 StartY=198.67 StartZ=0 EndX=703.577 EndY=177.659 EndZ=0
    g6: LineSegment StartX=678.466 StartY=184.836 StartZ=0 EndX=678.356 EndY=184.451 EndZ=0
    g7: LineSegment StartX=678.78 StartY=170.169 StartZ=0 EndX=678.902 EndY=169.787 EndZ=0
    g8: LineSegment StartX=656.289 StartY=159.141 StartZ=0 EndX=766.918 EndY=159.141 EndZ=0
    g9: LineSegment StartX=769.773 StartY=158.741 StartZ=0 EndX=656.289 EndY=158.741 EndZ=0
    g10: LineSegment StartX=656.289 StartY=158.741 StartZ=0 EndX=656.289 EndY=159.141 EndZ=0
    g11: LineSegment StartX=766.918 StartY=159.141 StartZ=0 EndX=702.889 EndY=177.44 EndZ=0
    g12: LineSegment StartX=657.884 StartY=190.302 StartZ=0 EndX=657.884 EndY=163.502 EndZ=0
    g13: LineSegment StartX=657.884 StartY=190.718 StartZ=0 EndX=702.883 EndY=177.858 EndZ=0
    g14: LineSegment StartX=657.884 StartY=163.082 StartZ=0 EndX=657.884 EndY=161.636 EndZ=0
    g15: LineSegment StartX=657.884 StartY=163.502 StartZ=0 EndX=702.195 EndY=177.638 EndZ=0
    g16: LineSegment StartX=702.883 StartY=177.858 StartZ=0 EndX=769.434 EndY=199.089 EndZ=0
    g17: LineSegment StartX=703.577 StartY=177.659 StartZ=0 EndX=769.773 EndY=158.741 EndZ=0
    g18: LineSegment StartX=702.889 StartY=177.44 StartZ=0 EndX=657.884 EndY=163.082 EndZ=0
    g19: LineSegment StartX=702.195 StartY=177.638 StartZ=0 EndX=657.884 EndY=190.302 EndZ=0
  constraints (36):
    c: Coincident(g0,g1)
    c: Coincident(g14,g2)
    c: Coincident(g2,g3)
    c: Coincident(g3,g0)
    c: Horizontal(g0)
    c: Horizontal(g2)
    c: Vertical(g1)
    c: Vertical(g3)
    c: DistanceX(g0,g0) = 0.3
    c: DistanceX(g2) = 657.584
    c: DistanceY(g2) = 161.636
    c: Coincident(g16,g4)
    c: Vertical(g4)
    c: Coincident(g4,g5)
    c: Distance(g6) = 0.4
    c: PointOnObject(g7,g5)
    c: Perpendicular(g5,g7)
    c: Distance(g7) = 0.4
    c: Coincident(g9,g10)
    c: Coincident(g10,g8)
    c: Horizontal(g8)
    c: Horizontal(g9)
    c: Vertical(g10)
    c: Coincident(g11,g8)
    c: Coincident(g17,g9)
    c: DistanceY(g10,g10) = 0.4
    c: DistanceX(g9) = 656.289
    c: DistanceY(g9) = 158.741
    c: Coincident(g19,g12)
    c: Coincident(g13,g1)
    c: Coincident(g18,g14)
    c: Coincident(g15,g12)
    c: Coincident(g13,g16)
    c: Coincident(g5,g17)
    c: Coincident(g11,g18)
    c: Coincident(g19,g15)
FEATURE [PartDesign::Pad] Pad003
  Direction = (0,-1,-2e-16)
  Length = 15
  Length2 = 10
  Midplane = true
  Placement = pos=(0,0,0) rot=(1,0,0;1.5708rad)
  Profile = -> Sketch030
  ReferenceAxis = -> Sketch030 [N_Axis]
  Type = 0
FEATURE [PartDesign::Body] Body005  label="Struct btm rudder"
  Group = -> [Sketch030,Pad003]
  Origin = -> Origin007
  Tip = -> Pad003
FEATURE [Sketcher::SketchObject] Sketch031
  AttachmentOffset = pos=(0,0,153) rot=(0,0,1;0rad)
  FullyConstrained = true
  MapMode = 5
  Placement = pos=(0,0,153) rot=(0,0,1;0rad)
  Support = -> [XY_Plane002]
  sketch-geometry (4):
    g0: LineSegment StartX=654.771 StartY=0.05 StartZ=0 EndX=779.771 EndY=0.05 EndZ=0
    g1: LineSegment StartX=779.771 StartY=0.05 StartZ=0 EndX=779.771 EndY=-0.05 EndZ=0
    g2: LineSegment StartX=779.771 StartY=-0.05 StartZ=0 EndX=654.771 EndY=-0.05 EndZ=0
    g3: LineSegment StartX=654.771 StartY=-0.05 StartZ=0 EndX=654.771 EndY=0.05 EndZ=0
  constraints (11):
    c: Coincident(g0,g1)
    c: Coincident(g1,g2)
    c: Coincident(g2,g3)
    c: Coincident(g3,g0)
    c: Horizontal(g0)
    c: Horizontal(g2)
    c: Vertical(g1)
    c: Symmetric(g0,g2,g-1)
    c: DistanceY(g3,g3) = 0.1
    c: DistanceX(g0) = 654.771
    c: DistanceX(g0,g0) = 125
FEATURE [PartDesign::Pocket] Pocket003
  BaseFeature = -> Pad001
  Direction = (0,0,-1)
  Length = 6
  Length2 = 5
  Placement = pos=(657.694,9e-14,142.303) rot=(-0.57735,0.57735,0.57735;4.18879rad)
  Profile = -> Sketch031
  ReferenceAxis = -> Sketch031 [N_Axis]
  Reversed = true
  Type = 0
FEATURE [PartDesign::Body] Body002  label="Rudder1"
  Group = -> [Sketch009,Sketch010,Sketch011,Sketch012,Sketch013,Sketch014,Sketch015,AdditiveLoft001,ShapeBinder,Sketch016,Sketch017,Sketch018,SubtractiveLoft001,ShapeBinder001,Sketch019,Pocket001,DatumPlane005,Sketch028,Pad001,Sketch031,Pocket003]
  Origin = -> Origin002
  Tip = -> Pocket003
FEATURE [Mesh::Feature] Mesh001  label="Struct btm rudder (Meshed)"
FEATURE [Mesh::Feature] Mesh002  label="TopRudder (Meshed)"
FEATURE [Mesh::Feature] Mesh003  label="Struct top rudder (Meshed)"
FEATURE [Sketcher::SketchObject] Sketch032
  AttachmentOffset = pos=(0,0,163) rot=(0,0,1;0rad)
  FullyConstrained = true
  MapMode = 5
  Placement = pos=(0,0,163) rot=(0,0,1;0rad)
  Support = -> [XY_Plane005]
  sketch-geometry (4):
    g0: LineSegment StartX=656.512 StartY=0.05 StartZ=0 EndX=781.512 EndY=0.05 EndZ=0
    g1: LineSegment StartX=781.512 StartY=0.05 StartZ=0 EndX=781.512 EndY=-0.05 EndZ=0
    g2: LineSegment StartX=781.512 StartY=-0.05 StartZ=0 EndX=656.512 EndY=-0.05 EndZ=0
    g3: LineSegment StartX=656.512 StartY=-0.05 StartZ=0 EndX=656.512 EndY=0.05 EndZ=0
  constraints (11):
    c: Coincident(g0,g1)
    c: Coincident(g1,g2)
    c: Coincident(g2,g3)
    c: Coincident(g3,g0)
    c: Horizontal(g0)
    c: Horizontal(g2)
    c: Vertical(g3)
    c: Symmetric(g1,g0,g-1)
    c: DistanceX(g0,g0) = 125
    c: DistanceY(g3,g3) = 0.1
    c: DistanceX(g0) = 656.512
FEATURE [PartDesign::Pocket] Pocket004
  BaseFeature = -> Pocket
  Direction = (0,0,-1)
  Length = 5
  Length2 = 5
  Profile = -> Sketch032
  ReferenceAxis = -> Sketch032 [N_Axis]
  Type = 0
FEATURE [PartDesign::Body] PocketBody
  BaseFeature = -> DatumPlane
  Group = -> [BaseFeature,Sketch004,AdditiveLoft,Sketch006,SubtractiveLoft,Sketch008,Pocket,Sketch032,Pocket004]
  Origin = -> Origin005
  Tip = -> Pocket004
FEATURE [App::Part] Part
  Group = -> [PocketBody]
  Origin = -> Origin004
FEATURE [Sketcher::SketchObject] Sketch033
  FullyConstrained = false
  MapMode = 5
  Placement = pos=(0,0,0) rot=(1,0,0;1.5708rad)
  Support = -> [XZ_Plane008]
  sketch-geometry (22):
    g0: LineSegment StartX=657.642 StartY=168.695 StartZ=0 EndX=657.942 EndY=168.695 EndZ=0
    g1: LineSegment StartX=657.942 StartY=168.695 StartZ=0 EndX=657.942 EndY=159.128 EndZ=0
    g2: LineSegment StartX=657.942 StartY=138.791 StartZ=0 EndX=657.642 EndY=138.791 EndZ=0
    g3: LineSegment StartX=657.642 StartY=138.791 StartZ=0 EndX=657.642 EndY=168.695 EndZ=0
    g4: LineSegment StartX=782.359 StartY=159.128 StartZ=0 EndX=782.359 EndY=158.728 EndZ=0
    g5: LineSegment StartX=782.359 StartY=158.728 StartZ=0 EndX=657.942 EndY=158.728 EndZ=0
    g6: LineSegment StartX=782.62 StartY=154.09 StartZ=0 EndX=782.831 EndY=153.708 EndZ=0
    g7: LineSegment StartX=782.831 StartY=153.708 StartZ=0 EndX=721.382 EndY=147.946 EndZ=0
    g8: LineSegment StartX=784.331 StartY=142.157 StartZ=0 EndX=783.264 EndY=141.853 EndZ=0
    g9: LineSegment StartX=783.264 StartY=141.853 StartZ=0 EndX=719.219 EndY=147.743 EndZ=0
    g10: LineSegment StartX=741.695 StartY=146.078 StartZ=0 EndX=741.659 EndY=145.68 EndZ=0
    g11: LineSegment StartX=744.702 StartY=150.535 StartZ=0 EndX=744.739 EndY=150.136 EndZ=0
    g12: LineSegment StartX=657.942 StartY=153.379 StartZ=0 EndX=657.942 EndY=142.399 EndZ=0
    g13: LineSegment StartX=657.942 StartY=153.78 StartZ=0 EndX=719.219 EndY=148.145 EndZ=0
    g14: LineSegment StartX=657.942 StartY=158.728 StartZ=0 EndX=657.942 EndY=153.78 EndZ=0
    g15: LineSegment StartX=657.942 StartY=159.128 StartZ=0 EndX=782.359 EndY=159.128 EndZ=0
    g16: LineSegment StartX=657.942 StartY=141.997 StartZ=0 EndX=657.942 EndY=138.791 EndZ=0
    g17: LineSegment StartX=657.942 StartY=142.399 StartZ=0 EndX=717.056 EndY=147.942 EndZ=0
    g18: LineSegment StartX=717.056 StartY=147.942 StartZ=0 EndX=657.942 EndY=153.379 EndZ=0
    g19: LineSegment StartX=719.219 StartY=148.145 StartZ=0 EndX=782.62 EndY=154.09 EndZ=0
    g20: LineSegment StartX=721.382 StartY=147.946 StartZ=0 EndX=784.331 EndY=142.157 EndZ=0
    g21: LineSegment StartX=719.219 StartY=147.743 StartZ=0 EndX=657.942 EndY=141.997 EndZ=0
  constraints (31):
    c: Coincident(g0,g1)
    c: Coincident(g16,g2)
    c: Coincident(g2,g3)
    c: Coincident(g3,g0)
    c: Horizontal(g0)
    c: Horizontal(g2)
    c: Vertical(g1)
    c: Vertical(g3)
    c: DistanceX(g0,g0) = 0.3
    c: Coincident(g15,g4)
    c: Coincident(g4,g5)
    c: Horizontal(g5)
    c: Vertical(g4)
    c: Coincident(g19,g6)
    c: Coincident(g6,g7)
    c: Coincident(g20,g8)
    c: Coincident(g8,g9)
    c: PointOnObject(g10,g9)
    c: PointOnObject(g11,g7)
    c: Equal(g10,g11)
    c: Distance(g11) = 0.4
    c: Coincident(g13,g14)
    c: Coincident(g18,g12)
    c: Coincident(g15,g1)
    c: Coincident(g5,g14)
    c: Coincident(g17,g12)
    c: Coincident(g21,g16)
    c: Coincident(g17,g18)
    c: Coincident(g13,g19)
    c: Coincident(g7,g20)
    c: Coincident(g21,g9)
FEATURE [PartDesign::Pad] Pad004
  Direction = (0,-1,2e-16)
  Length = 18
  Length2 = 10
  Midplane = true
  Placement = pos=(0,0,0) rot=(1,0,0;1.5708rad)
  Profile = -> Sketch033
  ReferenceAxis = -> Sketch033 [N_Axis]
  Type = 0
FEATURE [PartDesign::Body] Body006  label="Part Struct"
  Group = -> [Sketch033,Pad004]
  Origin = -> Origin008
  Tip = -> Pad004
FEATURE [Mesh::Feature] Mesh004  label="HingePart"
FEATURE [Mesh::Feature] Mesh005  label="HingePart Struct"
FEATURE [Mesh::Feature] Mesh006  label="Rudder1 (Meshed)001"
